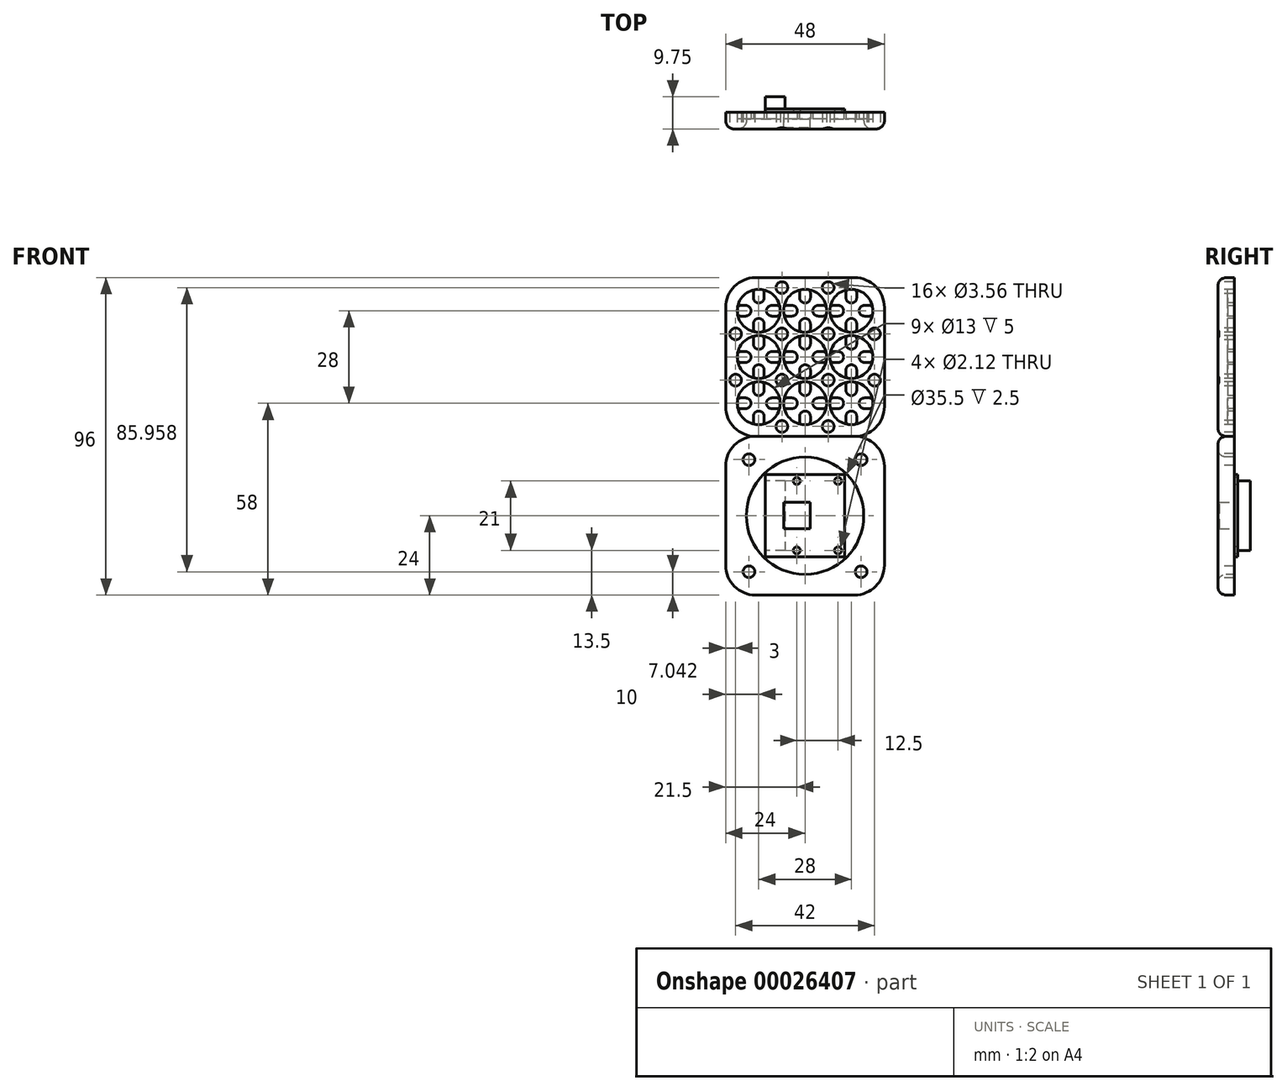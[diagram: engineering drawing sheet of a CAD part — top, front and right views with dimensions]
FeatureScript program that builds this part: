
annotation { "Feature Type Name" : "Feature", "Feature Type Description" : "" }
export const myFeature = defineFeature(function(context is Context, id is Id, definition is map)
    precondition{}
    {
        {
            var Q0;
            Q0=qCreatedBy(makeId("Front.planeOp"),FACE);
            var sketch = newSketch(context, id + "F0", { "sketchPlane" : qUnion([Q0])});
            skCircle(sketch, "E0", {"center": v(0, 0) * mm, "radius": 6.5 * mm});
            skCircle(sketch, "E1", {"center": v(0, 0) * mm, "radius": 7 * mm, "construction": true});
            skLineSegment(sketch, "E2", {"start": v(0, 7) * mm, "end": v(0, 14) * mm, "construction": true});
            skCircle(sketch, "E3", {"center": v(0, 14) * mm, "radius": 7 * mm, "construction": true});
            skCircle(sketch, "E4", {"center": v(0, 14) * mm, "radius": 6.5 * mm});
            skLineSegment(sketch, "E5", {"start": v(0, -7) * mm, "end": v(0, -14) * mm, "construction": true});
            skCircle(sketch, "E6", {"center": v(0, -14) * mm, "radius": 7 * mm, "construction": true});
            skCircle(sketch, "E7", {"center": v(0, -14) * mm, "radius": 6.5 * mm});
            skLineSegment(sketch, "E8", {"start": v(-7, 14) * mm, "end": v(-14, 14) * mm, "construction": true});
            skLineSegment(sketch, "E9", {"start": v(-7, 0) * mm, "end": v(-14, 0) * mm, "construction": true});
            skLineSegment(sketch, "E10", {"start": v(-7, -14) * mm, "end": v(-14, -14) * mm, "construction": true});
            skLineSegment(sketch, "E11", {"start": v(7, 14) * mm, "end": v(14, 14) * mm, "construction": true});
            skLineSegment(sketch, "E12", {"start": v(7, 0) * mm, "end": v(14, 0) * mm, "construction": true});
            skLineSegment(sketch, "E13", {"start": v(7, -14) * mm, "end": v(14, -14) * mm, "construction": true});
            skCircle(sketch, "E14", {"center": v(14, 14) * mm, "radius": 7 * mm, "construction": true});
            skCircle(sketch, "E15", {"center": v(14, 0) * mm, "radius": 7 * mm, "construction": true});
            skCircle(sketch, "E16", {"center": v(14, -14) * mm, "radius": 7 * mm, "construction": true});
            skCircle(sketch, "E17", {"center": v(-14, -14) * mm, "radius": 7 * mm, "construction": true});
            skCircle(sketch, "E18", {"center": v(-14, 0) * mm, "radius": 7 * mm, "construction": true});
            skCircle(sketch, "E19", {"center": v(-14, 14) * mm, "radius": 7 * mm, "construction": true});
            skCircle(sketch, "E20", {"center": v(-14, 14) * mm, "radius": 6.5 * mm});
            skCircle(sketch, "E21", {"center": v(-14, 0) * mm, "radius": 6.5 * mm});
            skCircle(sketch, "E22", {"center": v(-14, -14) * mm, "radius": 6.5 * mm});
            skCircle(sketch, "E23", {"center": v(14, -14) * mm, "radius": 6.5 * mm});
            skCircle(sketch, "E24", {"center": v(14, 0) * mm, "radius": 6.5 * mm});
            skCircle(sketch, "E25", {"center": v(14, 14) * mm, "radius": 6.5 * mm});
            skLineSegment(sketch, "E26", {"start": v(-14, 14) * mm, "end": v(-21, 14) * mm, "construction": true});
            skLineSegment(sketch, "E27", {"start": v(-14, 14) * mm, "end": v(-14, 21) * mm, "construction": true});
            skLineSegment(sketch, "E28", {"start": v(14, -14) * mm, "end": v(14, -21) * mm, "construction": true});
            skLineSegment(sketch, "E29", {"start": v(14, -14) * mm, "end": v(21, -14) * mm, "construction": true});
            skLineSegment(sketch, "E30.rect.bottom", {"start": v(-21, 21) * mm, "end": v(21, 21) * mm, "construction": true});
            skLineSegment(sketch, "E30.rect.top", {"start": v(-12, -21) * mm, "end": v(21, -21) * mm, "construction": true});
            skLineSegment(sketch, "E30.rect.left", {"start": v(-21, 21) * mm, "end": v(-21, -12) * mm, "construction": true});
            skLineSegment(sketch, "E30.rect.right", {"start": v(21, 21) * mm, "end": v(21, -21) * mm, "construction": true});
            skLineSegment(sketch, "E31.0", {"start": v(-24, 15) * mm, "end": v(-24, -15) * mm});
            skLineSegment(sketch, "E31.1", {"start": v(-15, 24) * mm, "end": v(15, 24) * mm});
            skLineSegment(sketch, "E31.2", {"start": v(24, 15) * mm, "end": v(24, -15) * mm});
            skLineSegment(sketch, "E31.3", {"start": v(-15, -24) * mm, "end": v(15, -24) * mm});
            skPoint(sketch, "E32.visualSharp", {"position": v(-24, -24) * mm});
            skArc(sketch, "E32.filletArc", {"start": v(-24, -15) * mm, "mid": v(-21.36, -21.36) * mm, "end": v(-15, -24) * mm});
            skPoint(sketch, "E33.visualSharp", {"position": v(-24, 24) * mm});
            skArc(sketch, "E33.filletArc", {"start": v(-15, 24) * mm, "mid": v(-21.36, 21.36) * mm, "end": v(-24, 15) * mm});
            skPoint(sketch, "E34.visualSharp", {"position": v(24, 24) * mm});
            skArc(sketch, "E34.filletArc", {"start": v(24, 15) * mm, "mid": v(21.36, 21.36) * mm, "end": v(15, 24) * mm});
            skPoint(sketch, "E35.visualSharp", {"position": v(24, -24) * mm});
            skArc(sketch, "E35.filletArc", {"start": v(15, -24) * mm, "mid": v(21.36, -21.36) * mm, "end": v(24, -15) * mm});
            skPoint(sketch, "E36.visualSharp", {"position": v(-21, -21) * mm});
            skArc(sketch, "E36.filletArc", {"start": v(-21, -12) * mm, "mid": v(-18.36, -18.36) * mm, "end": v(-12, -21) * mm, "construction": true});
            skLineSegment(sketch, "E37", {"start": v(7, -14) * mm, "end": v(7, 14) * mm, "construction": true});
            skLineSegment(sketch, "E38", {"start": v(14, -7) * mm, "end": v(-14, -7) * mm, "construction": true});
            skLineSegment(sketch, "E39", {"start": v(-7, -14) * mm, "end": v(-7, 14) * mm, "construction": true});
            skLineSegment(sketch, "E40", {"start": v(14, -7) * mm, "end": v(24, -7) * mm, "construction": true});
            skLineSegment(sketch, "E41", {"start": v(7, -14) * mm, "end": v(7, -24) * mm, "construction": true});
            skLineSegment(sketch, "E42", {"start": v(-7, -14) * mm, "end": v(-7, -24) * mm, "construction": true});
            skLineSegment(sketch, "E43", {"start": v(-14, -7) * mm, "end": v(-24, -7) * mm, "construction": true});
            skLineSegment(sketch, "E44", {"start": v(14, 7) * mm, "end": v(-14, 7) * mm, "construction": true});
            skLineSegment(sketch, "E45", {"start": v(14, 7) * mm, "end": v(24, 7) * mm, "construction": true});
            skLineSegment(sketch, "E46", {"start": v(7, 14) * mm, "end": v(7, 24) * mm, "construction": true});
            skLineSegment(sketch, "E47", {"start": v(-7, 14) * mm, "end": v(-7, 24) * mm, "construction": true});
            skLineSegment(sketch, "E48", {"start": v(-14, 7) * mm, "end": v(-24, 7) * mm, "construction": true});
            skCircle(sketch, "E49", {"center": v(7, -7) * mm, "radius": 1.78 * mm});
            skCircle(sketch, "E50", {"center": v(-7, -7) * mm, "radius": 1.78 * mm});
            skCircle(sketch, "E51", {"center": v(-7, 7) * mm, "radius": 1.78 * mm});
            skCircle(sketch, "E52", {"center": v(7, 7) * mm, "radius": 1.78 * mm});
            skCircle(sketch, "E53", {"center": v(-7, -21) * mm, "radius": 1.78 * mm});
            skCircle(sketch, "E54", {"center": v(7, -21) * mm, "radius": 1.78 * mm});
            skCircle(sketch, "E55", {"center": v(21, -7) * mm, "radius": 1.78 * mm});
            skCircle(sketch, "E56", {"center": v(21, 7) * mm, "radius": 1.78 * mm});
            skCircle(sketch, "E57", {"center": v(7, 21) * mm, "radius": 1.78 * mm});
            skCircle(sketch, "E58", {"center": v(-7, 21) * mm, "radius": 1.78 * mm});
            skCircle(sketch, "E59", {"center": v(-21, 7) * mm, "radius": 1.78 * mm});
            skCircle(sketch, "E60", {"center": v(-21, -7) * mm, "radius": 1.78 * mm});
            skSolve(sketch);
        }
        {
            var Q0;
            Q0=makeQuery(id+"F0.imprint","IMPRINT",FACE,{"disambiguationData":[TD([[makeQuery(id+"F0.imprint","IMPRINT",EDGE,{"derivedFrom":sQuery(id+"F0.wireOp",EDGE,"E0")}),-1.0]])]});
            var Q1;
            Q1=makeQuery(id+"F0.imprint","IMPRINT",FACE,{"disambiguationData":[TD([[makeQuery(id+"F0.imprint","IMPRINT",EDGE,{"derivedFrom":sQuery(id+"F0.wireOp",EDGE,"E21")}),1.0]])]});
            var Q2;
            Q2=makeQuery(id+"F0.imprint","IMPRINT",FACE,{"disambiguationData":[TD([[makeQuery(id+"F0.imprint","IMPRINT",EDGE,{"derivedFrom":sQuery(id+"F0.wireOp",EDGE,"E22")}),1.0]])]});
            var Q3;
            Q3=makeQuery(id+"F0.imprint","IMPRINT",FACE,{"disambiguationData":[TD([[makeQuery(id+"F0.imprint","IMPRINT",EDGE,{"derivedFrom":sQuery(id+"F0.wireOp",EDGE,"E7")}),1.0]])]});
            var Q4;
            Q4=makeQuery(id+"F0.imprint","IMPRINT",FACE,{"disambiguationData":[TD([[makeQuery(id+"F0.imprint","IMPRINT",EDGE,{"derivedFrom":sQuery(id+"F0.wireOp",EDGE,"E0")}),1.0]])]});
            var Q5;
            Q5=makeQuery(id+"F0.imprint","IMPRINT",FACE,{"disambiguationData":[TD([[makeQuery(id+"F0.imprint","IMPRINT",EDGE,{"derivedFrom":sQuery(id+"F0.wireOp",EDGE,"E20")}),1.0]])]});
            var Q6;
            Q6=makeQuery(id+"F0.imprint","IMPRINT",FACE,{"disambiguationData":[TD([[makeQuery(id+"F0.imprint","IMPRINT",EDGE,{"derivedFrom":sQuery(id+"F0.wireOp",EDGE,"E4")}),1.0]])]});
            var Q7;
            Q7=makeQuery(id+"F0.imprint","IMPRINT",FACE,{"disambiguationData":[TD([[makeQuery(id+"F0.imprint","IMPRINT",EDGE,{"derivedFrom":sQuery(id+"F0.wireOp",EDGE,"E25")}),1.0]])]});
            var Q8;
            Q8=makeQuery(id+"F0.imprint","IMPRINT",FACE,{"disambiguationData":[TD([[makeQuery(id+"F0.imprint","IMPRINT",EDGE,{"derivedFrom":sQuery(id+"F0.wireOp",EDGE,"E24")}),1.0]])]});
            var Q9;
            Q9=makeQuery(id+"F0.imprint","IMPRINT",FACE,{"disambiguationData":[TD([[makeQuery(id+"F0.imprint","IMPRINT",EDGE,{"derivedFrom":sQuery(id+"F0.wireOp",EDGE,"E23")}),1.0]])]});
            extrude(context, id + "F1", {"entities" : qUnion([Q0, Q1, Q2, Q3, Q4, Q5, Q6, Q7, Q8, Q9]), "oppositeDirection" : true, "depth" : 5 * mm});
        }
        {
            var Q0;
            Q0=makeQuery(id+"F0.imprint","IMPRINT",FACE,{"disambiguationData":[TD([[makeQuery(id+"F0.imprint","IMPRINT",EDGE,{"derivedFrom":sQuery(id+"F0.wireOp",EDGE,"E22")}),1.0]])]});
            var Q1;
            Q1=makeQuery(id+"F0.imprint","IMPRINT",FACE,{"disambiguationData":[TD([[makeQuery(id+"F0.imprint","IMPRINT",EDGE,{"derivedFrom":sQuery(id+"F0.wireOp",EDGE,"E21")}),1.0]])]});
            var Q2;
            Q2=makeQuery(id+"F0.imprint","IMPRINT",FACE,{"disambiguationData":[TD([[makeQuery(id+"F0.imprint","IMPRINT",EDGE,{"derivedFrom":sQuery(id+"F0.wireOp",EDGE,"E20")}),1.0]])]});
            var Q3;
            Q3=makeQuery(id+"F0.imprint","IMPRINT",FACE,{"disambiguationData":[TD([[makeQuery(id+"F0.imprint","IMPRINT",EDGE,{"derivedFrom":sQuery(id+"F0.wireOp",EDGE,"E4")}),1.0]])]});
            var Q4;
            Q4=makeQuery(id+"F0.imprint","IMPRINT",FACE,{"disambiguationData":[TD([[makeQuery(id+"F0.imprint","IMPRINT",EDGE,{"derivedFrom":sQuery(id+"F0.wireOp",EDGE,"E25")}),1.0]])]});
            var Q5;
            Q5=makeQuery(id+"F0.imprint","IMPRINT",FACE,{"disambiguationData":[TD([[makeQuery(id+"F0.imprint","IMPRINT",EDGE,{"derivedFrom":sQuery(id+"F0.wireOp",EDGE,"E24")}),1.0]])]});
            var Q6;
            Q6=makeQuery(id+"F0.imprint","IMPRINT",FACE,{"disambiguationData":[TD([[makeQuery(id+"F0.imprint","IMPRINT",EDGE,{"derivedFrom":sQuery(id+"F0.wireOp",EDGE,"E23")}),1.0]])]});
            var Q7;
            Q7=makeQuery(id+"F0.imprint","IMPRINT",FACE,{"disambiguationData":[TD([[makeQuery(id+"F0.imprint","IMPRINT",EDGE,{"derivedFrom":sQuery(id+"F0.wireOp",EDGE,"E7")}),1.0]])]});
            var Q8;
            Q8=makeQuery(id+"F0.imprint","IMPRINT",FACE,{"disambiguationData":[TD([[makeQuery(id+"F0.imprint","IMPRINT",EDGE,{"derivedFrom":sQuery(id+"F0.wireOp",EDGE,"E0")}),1.0]])]});
            extrude(context, id + "F2", {"entities" : qUnion([Q0, Q1, Q2, Q3, Q4, Q5, Q6, Q7, Q8]), "operationType" : NewBodyOperationType.REMOVE, "oppositeDirection" : true, "depth" : 3 * mm});
        }
        {
            var Q0;
            Q0=makeQuery(id+"F1.opExtrude","CAP_EDGE",EDGE,{"disambiguationData":[OSD([sQuery(id+"F0.wireOp",EDGE,"E31.3")])],"isStart":true});
            fillet(context, id + "F3", {"entities" : qUnion([Q0]), "radius" : 2.5 * mm, "tangentPropagation" : true, "allowEdgeOverflow" : false});
        }
        {
            var Q0;
            Q0=makeQuery(id+"F0.imprint","IMPRINT",FACE,{"disambiguationData":[TD([[makeQuery(id+"F0.imprint","IMPRINT",EDGE,{"derivedFrom":sQuery(id+"F0.wireOp",EDGE,"E0")}),1.0]])]});
            var sketch = newSketch(context, id + "F4", { "sketchPlane" : qUnion([Q0])});
            skCircle(sketch, "E61.0", {"center": v(-14, 14) * mm, "radius": 6.5 * mm, "construction": true});
            skCircle(sketch, "E62.0", {"center": v(0, 14) * mm, "radius": 6.5 * mm, "construction": true});
            skCircle(sketch, "E63.0", {"center": v(14, 14) * mm, "radius": 6.5 * mm, "construction": true});
            skCircle(sketch, "E64.0", {"center": v(-14, 0) * mm, "radius": 6.5 * mm, "construction": true});
            skCircle(sketch, "E65.0", {"center": v(0, 0) * mm, "radius": 6.5 * mm, "construction": true});
            skCircle(sketch, "E66.0", {"center": v(14, 0) * mm, "radius": 6.5 * mm, "construction": true});
            skCircle(sketch, "E67.0", {"center": v(14, -14) * mm, "radius": 6.5 * mm, "construction": true});
            skCircle(sketch, "E68.0", {"center": v(0, -14) * mm, "radius": 6.5 * mm, "construction": true});
            skCircle(sketch, "E69.0", {"center": v(-14, -14) * mm, "radius": 6.5 * mm, "construction": true});
            skLineSegment(sketch, "E70", {"start": v(0, 0) * mm, "end": v(0, 6.5) * mm, "construction": true});
            skLineSegment(sketch, "E71", {"start": v(0, 0) * mm, "end": v(0, -6.5) * mm, "construction": true});
            skLineSegment(sketch, "E72", {"start": v(0, 0) * mm, "end": v(6.5, 0) * mm, "construction": true});
            skLineSegment(sketch, "E73", {"start": v(0, 0) * mm, "end": v(-6.5, 0) * mm, "construction": true});
            skLineSegment(sketch, "E74", {"start": v(0, 3.25) * mm, "end": v(-3.25, 0) * mm, "construction": true});
            skLineSegment(sketch, "E75", {"start": v(-3.25, 0) * mm, "end": v(0, -3.25) * mm, "construction": true});
            skLineSegment(sketch, "E76", {"start": v(0, -3.25) * mm, "end": v(3.25, 0) * mm, "construction": true});
            skLineSegment(sketch, "E77", {"start": v(3.25, 0) * mm, "end": v(0, 3.25) * mm, "construction": true});
            skLineSegment(sketch, "E78", {"start": v(1.62, 1.63) * mm, "end": v(1.62, 6.3) * mm, "construction": true});
            skLineSegment(sketch, "E79", {"start": v(-1.63, 1.63) * mm, "end": v(-1.63, 6.3) * mm, "construction": true});
            skLineSegment(sketch, "E80", {"start": v(1.62, 1.63) * mm, "end": v(6.3, 1.63) * mm, "construction": true});
            skLineSegment(sketch, "E81", {"start": v(1.63, -1.63) * mm, "end": v(6.3, -1.63) * mm, "construction": true});
            skLineSegment(sketch, "E82", {"start": v(1.63, -1.63) * mm, "end": v(1.63, -6.3) * mm, "construction": true});
            skLineSegment(sketch, "E83", {"start": v(-1.63, -1.62) * mm, "end": v(-1.63, -6.3) * mm, "construction": true});
            skLineSegment(sketch, "E84", {"start": v(-1.63, -1.62) * mm, "end": v(-6.3, -1.62) * mm, "construction": true});
            skLineSegment(sketch, "E85", {"start": v(-1.63, 1.63) * mm, "end": v(-6.3, 1.63) * mm, "construction": true});
            skLineSegment(sketch, "E86", {"start": v(1.63, 3.96) * mm, "end": v(-1.63, 3.96) * mm, "construction": true});
            skLineSegment(sketch, "E87", {"start": v(3.96, 1.63) * mm, "end": v(3.96, -1.63) * mm, "construction": true});
            skLineSegment(sketch, "E88", {"start": v(1.63, -3.96) * mm, "end": v(-1.63, -3.96) * mm, "construction": true});
            skLineSegment(sketch, "E89", {"start": v(-3.96, 1.63) * mm, "end": v(-3.96, -1.62) * mm, "construction": true});
            skCircle(sketch, "E90", {"center": v(3.96, 0) * mm, "radius": 1.63 * mm, "construction": true});
            skCircle(sketch, "E91", {"center": v(0, 3.96) * mm, "radius": 1.63 * mm, "construction": true});
            skCircle(sketch, "E92", {"center": v(-3.96, 0) * mm, "radius": 1.63 * mm, "construction": true});
            skCircle(sketch, "E93", {"center": v(0, -3.96) * mm, "radius": 1.63 * mm, "construction": true});
            skLineSegment(sketch, "E94", {"start": v(6.3, 1.63) * mm, "end": v(3.96, 1.63) * mm});
            skLineSegment(sketch, "E95", {"start": v(6.3, -1.63) * mm, "end": v(3.96, -1.63) * mm});
            skArc(sketch, "E96", {"start": v(6.3, -1.63) * mm, "mid": v(6.5, 0) * mm, "end": v(6.3, 1.63) * mm});
            skArc(sketch, "E97", {"start": v(3.96, 1.63) * mm, "mid": v(2.33, 0) * mm, "end": v(3.96, -1.63) * mm});
            skArc(sketch, "E98", {"start": v(-1.63, 3.96) * mm, "mid": v(0, 2.33) * mm, "end": v(1.63, 3.96) * mm});
            skArc(sketch, "E99", {"start": v(1.63, 6.3) * mm, "mid": v(0, 6.5) * mm, "end": v(-1.63, 6.3) * mm});
            skLineSegment(sketch, "E100", {"start": v(1.63, 6.3) * mm, "end": v(1.63, 3.96) * mm});
            skLineSegment(sketch, "E101", {"start": v(-1.63, 6.3) * mm, "end": v(-1.63, 3.96) * mm});
            skLineSegment(sketch, "E102", {"start": v(1.63, -3.96) * mm, "end": v(1.63, -6.3) * mm});
            skLineSegment(sketch, "E103", {"start": v(-1.63, -6.3) * mm, "end": v(-1.63, -3.96) * mm});
            skLineSegment(sketch, "E104", {"start": v(-3.96, -1.62) * mm, "end": v(-6.3, -1.62) * mm});
            skLineSegment(sketch, "E105", {"start": v(-3.96, 1.63) * mm, "end": v(-6.3, 1.63) * mm});
            skArc(sketch, "E106", {"start": v(-3.96, -1.62) * mm, "mid": v(-2.33, 0) * mm, "end": v(-3.96, 1.63) * mm});
            skArc(sketch, "E107", {"start": v(-6.3, 1.62) * mm, "mid": v(-6.5, 0) * mm, "end": v(-6.3, -1.62) * mm});
            skArc(sketch, "E108", {"start": v(1.63, -3.96) * mm, "mid": v(0, -2.33) * mm, "end": v(-1.63, -3.96) * mm});
            skArc(sketch, "E109", {"start": v(-1.63, -6.3) * mm, "mid": v(0, -6.5) * mm, "end": v(1.63, -6.3) * mm});
            skLineSegment(sketch, "E110.1.0.0", {"start": v(20.3, 1.63) * mm, "end": v(17.96, 1.63) * mm});
            skArc(sketch, "E110.1.0.1", {"start": v(20.3, -1.63) * mm, "mid": v(20.5, 0) * mm, "end": v(20.3, 1.62) * mm});
            skLineSegment(sketch, "E110.1.0.2", {"start": v(20.3, -1.63) * mm, "end": v(17.96, -1.63) * mm});
            skArc(sketch, "E110.1.0.3", {"start": v(17.96, 1.63) * mm, "mid": v(16.33, 0) * mm, "end": v(17.96, -1.63) * mm});
            skArc(sketch, "E110.1.0.4", {"start": v(12.38, 3.96) * mm, "mid": v(14, 2.33) * mm, "end": v(15.62, 3.96) * mm});
            skLineSegment(sketch, "E110.1.0.5", {"start": v(15.62, 6.3) * mm, "end": v(15.62, 3.96) * mm});
            skLineSegment(sketch, "E110.1.0.6", {"start": v(12.38, 6.3) * mm, "end": v(12.38, 3.96) * mm});
            skArc(sketch, "E110.1.0.7", {"start": v(15.62, 6.3) * mm, "mid": v(14, 6.5) * mm, "end": v(12.37, 6.3) * mm});
            skLineSegment(sketch, "E110.1.0.8", {"start": v(10.04, 1.63) * mm, "end": v(7.7, 1.63) * mm});
            skArc(sketch, "E110.1.0.9", {"start": v(10.04, -1.62) * mm, "mid": v(11.67, 0) * mm, "end": v(10.04, 1.63) * mm});
            skLineSegment(sketch, "E110.1.0.10", {"start": v(10.04, -1.62) * mm, "end": v(7.7, -1.62) * mm});
            skArc(sketch, "E110.1.0.11", {"start": v(7.7, 1.62) * mm, "mid": v(7.5, 0) * mm, "end": v(7.7, -1.62) * mm});
            skArc(sketch, "E110.1.0.12", {"start": v(15.62, -3.96) * mm, "mid": v(14, -2.33) * mm, "end": v(12.38, -3.96) * mm});
            skLineSegment(sketch, "E110.1.0.13", {"start": v(15.62, -3.96) * mm, "end": v(15.62, -6.3) * mm});
            skLineSegment(sketch, "E110.1.0.14", {"start": v(12.38, -6.3) * mm, "end": v(12.38, -3.96) * mm});
            skArc(sketch, "E110.1.0.15", {"start": v(12.37, -6.3) * mm, "mid": v(14, -6.5) * mm, "end": v(15.62, -6.3) * mm});
            skLineSegment(sketch, "E110.direction1", {"start": v(3.96, 1.63) * mm, "end": v(17.96, 1.63) * mm, "construction": true});
            skArc(sketch, "E111.1.0.0", {"start": v(-10.04, 1.63) * mm, "mid": v(-11.67, 0) * mm, "end": v(-10.04, -1.63) * mm});
            skLineSegment(sketch, "E111.1.0.1", {"start": v(-7.7, 1.63) * mm, "end": v(-10.04, 1.63) * mm});
            skArc(sketch, "E111.1.0.2", {"start": v(-7.7, -1.63) * mm, "mid": v(-7.5, 0) * mm, "end": v(-7.7, 1.63) * mm});
            skLineSegment(sketch, "E111.1.0.3", {"start": v(-7.7, -1.63) * mm, "end": v(-10.04, -1.63) * mm});
            skArc(sketch, "E111.1.0.4", {"start": v(-15.62, 3.96) * mm, "mid": v(-14, 2.33) * mm, "end": v(-12.38, 3.96) * mm});
            skLineSegment(sketch, "E111.1.0.5", {"start": v(-12.38, 6.3) * mm, "end": v(-12.38, 3.96) * mm});
            skArc(sketch, "E111.1.0.6", {"start": v(-12.38, 6.3) * mm, "mid": v(-14, 6.5) * mm, "end": v(-15.62, 6.3) * mm});
            skLineSegment(sketch, "E111.1.0.7", {"start": v(-15.62, 6.3) * mm, "end": v(-15.62, 3.96) * mm});
            skLineSegment(sketch, "E111.1.0.8", {"start": v(-17.96, 1.63) * mm, "end": v(-20.3, 1.63) * mm});
            skArc(sketch, "E111.1.0.9", {"start": v(-17.96, -1.62) * mm, "mid": v(-16.33, 0) * mm, "end": v(-17.96, 1.63) * mm});
            skLineSegment(sketch, "E111.1.0.10", {"start": v(-17.96, -1.62) * mm, "end": v(-20.3, -1.62) * mm});
            skArc(sketch, "E111.1.0.11", {"start": v(-20.3, 1.62) * mm, "mid": v(-20.5, 0) * mm, "end": v(-20.3, -1.62) * mm});
            skArc(sketch, "E111.1.0.12", {"start": v(-12.38, -3.96) * mm, "mid": v(-14, -2.33) * mm, "end": v(-15.62, -3.96) * mm});
            skLineSegment(sketch, "E111.1.0.13", {"start": v(-12.38, -3.96) * mm, "end": v(-12.38, -6.3) * mm});
            skArc(sketch, "E111.1.0.14", {"start": v(-15.62, -6.3) * mm, "mid": v(-14, -6.5) * mm, "end": v(-12.38, -6.3) * mm});
            skLineSegment(sketch, "E111.1.0.15", {"start": v(-15.62, -6.3) * mm, "end": v(-15.62, -3.96) * mm});
            skLineSegment(sketch, "E111.direction1", {"start": v(3.96, -1.63) * mm, "end": v(-10.04, -1.63) * mm, "construction": true});
            skCircle(sketch, "E112.0", {"center": v(21, 7) * mm, "radius": 1.78 * mm, "construction": true});
            skCircle(sketch, "E113.0", {"center": v(21, -7) * mm, "radius": 1.78 * mm, "construction": true});
            skCircle(sketch, "E114.0", {"center": v(7, 21) * mm, "radius": 1.78 * mm, "construction": true});
            skCircle(sketch, "E115.0", {"center": v(-7, 21) * mm, "radius": 1.78 * mm, "construction": true});
            skCircle(sketch, "E116.0", {"center": v(7, 7) * mm, "radius": 1.78 * mm, "construction": true});
            skCircle(sketch, "E117.0", {"center": v(-7, 7) * mm, "radius": 1.78 * mm, "construction": true});
            skCircle(sketch, "E118.0", {"center": v(-21, 7) * mm, "radius": 1.78 * mm, "construction": true});
            skCircle(sketch, "E119.0", {"center": v(-21, -7) * mm, "radius": 1.78 * mm, "construction": true});
            skCircle(sketch, "E120.0", {"center": v(-7, -7) * mm, "radius": 1.78 * mm, "construction": true});
            skCircle(sketch, "E121.0", {"center": v(7, -7) * mm, "radius": 1.78 * mm, "construction": true});
            skCircle(sketch, "E122.0", {"center": v(7, -21) * mm, "radius": 1.78 * mm, "construction": true});
            skCircle(sketch, "E123.0", {"center": v(-7, -21) * mm, "radius": 1.78 * mm, "construction": true});
            skLineSegment(sketch, "E124", {"start": v(14, -14) * mm, "end": v(-14, -14) * mm, "construction": true});
            skLineSegment(sketch, "E125", {"start": v(14, 14) * mm, "end": v(-14, 14) * mm, "construction": true});
            skLineSegment(sketch, "E126", {"start": v(14, 14) * mm, "end": v(14, -14) * mm, "construction": true});
            skLineSegment(sketch, "E127", {"start": v(-14, -14) * mm, "end": v(-14, 14) * mm, "construction": true});
            skLineSegment(sketch, "E128", {"start": v(21, -7) * mm, "end": v(-21, -7) * mm, "construction": true});
            skLineSegment(sketch, "E129", {"start": v(21, 7) * mm, "end": v(-21, 7) * mm, "construction": true});
            skLineSegment(sketch, "E130", {"start": v(7, 21) * mm, "end": v(7, -21) * mm, "construction": true});
            skLineSegment(sketch, "E131", {"start": v(-7, 21) * mm, "end": v(-7, -21) * mm, "construction": true});
            skArc(sketch, "E132.MirrorCS", {"start": v(7.7, 12.38) * mm, "mid": v(7.5, 14) * mm, "end": v(7.7, 15.62) * mm});
            skLineSegment(sketch, "E133.MirrorCS", {"start": v(10.04, 15.62) * mm, "end": v(7.7, 15.62) * mm});
            skArc(sketch, "E134.MirrorCS", {"start": v(10.04, 15.62) * mm, "mid": v(11.67, 14) * mm, "end": v(10.04, 12.38) * mm});
            skLineSegment(sketch, "E135.MirrorCS", {"start": v(10.04, 12.38) * mm, "end": v(7.7, 12.38) * mm});
            skArc(sketch, "E136.MirrorCS", {"start": v(12.38, 10.04) * mm, "mid": v(14, 11.67) * mm, "end": v(15.62, 10.04) * mm});
            skArc(sketch, "E137.MirrorCS", {"start": v(15.62, 7.7) * mm, "mid": v(14, 7.5) * mm, "end": v(12.37, 7.7) * mm});
            skLineSegment(sketch, "E138.MirrorCS", {"start": v(15.62, 7.7) * mm, "end": v(15.62, 10.04) * mm});
            skLineSegment(sketch, "E139.MirrorCS", {"start": v(12.38, 7.7) * mm, "end": v(12.38, 10.04) * mm});
            skLineSegment(sketch, "E140.MirrorCS", {"start": v(12.38, 20.3) * mm, "end": v(12.38, 17.96) * mm});
            skArc(sketch, "E141.MirrorCS", {"start": v(12.37, 20.3) * mm, "mid": v(14, 20.5) * mm, "end": v(15.62, 20.3) * mm});
            skLineSegment(sketch, "E142.MirrorCS", {"start": v(15.62, 17.96) * mm, "end": v(15.62, 20.3) * mm});
            skArc(sketch, "E143.MirrorCS", {"start": v(15.62, 17.96) * mm, "mid": v(14, 16.33) * mm, "end": v(12.38, 17.96) * mm});
            skArc(sketch, "E144.MirrorCS", {"start": v(17.96, 12.38) * mm, "mid": v(16.33, 14) * mm, "end": v(17.96, 15.62) * mm});
            skLineSegment(sketch, "E145.MirrorCS", {"start": v(20.3, 15.62) * mm, "end": v(17.96, 15.62) * mm});
            skLineSegment(sketch, "E146.MirrorCS", {"start": v(20.3, 12.38) * mm, "end": v(17.96, 12.38) * mm});
            skArc(sketch, "E147.MirrorCS", {"start": v(20.3, 15.62) * mm, "mid": v(20.5, 14) * mm, "end": v(20.3, 12.38) * mm});
            skLineSegment(sketch, "E148.MirrorCS", {"start": v(6.3, 12.38) * mm, "end": v(3.96, 12.38) * mm});
            skArc(sketch, "E149.MirrorCS", {"start": v(3.96, 12.38) * mm, "mid": v(2.33, 14) * mm, "end": v(3.96, 15.62) * mm});
            skArc(sketch, "E150.MirrorCS", {"start": v(6.3, 15.62) * mm, "mid": v(6.5, 14) * mm, "end": v(6.3, 12.38) * mm});
            skLineSegment(sketch, "E151.MirrorCS", {"start": v(6.3, 15.62) * mm, "end": v(3.96, 15.62) * mm});
            skLineSegment(sketch, "E152.MirrorCS", {"start": v(1.63, 7.7) * mm, "end": v(1.63, 10.04) * mm});
            skArc(sketch, "E153.MirrorCS", {"start": v(1.63, 7.7) * mm, "mid": v(0, 7.5) * mm, "end": v(-1.63, 7.7) * mm});
            skLineSegment(sketch, "E154.MirrorCS", {"start": v(-1.63, 7.7) * mm, "end": v(-1.63, 10.04) * mm});
            skArc(sketch, "E155.MirrorCS", {"start": v(-1.63, 10.04) * mm, "mid": v(0, 11.67) * mm, "end": v(1.63, 10.04) * mm});
            skArc(sketch, "E156.MirrorCS", {"start": v(1.63, 17.96) * mm, "mid": v(0, 16.33) * mm, "end": v(-1.63, 17.96) * mm});
            skLineSegment(sketch, "E157.MirrorCS", {"start": v(1.63, 17.96) * mm, "end": v(1.63, 20.3) * mm});
            skLineSegment(sketch, "E158.MirrorCS", {"start": v(-1.63, 20.3) * mm, "end": v(-1.63, 17.96) * mm});
            skArc(sketch, "E159.MirrorCS", {"start": v(-1.63, 20.3) * mm, "mid": v(0, 20.5) * mm, "end": v(1.63, 20.3) * mm});
            skLineSegment(sketch, "E160.MirrorCS", {"start": v(-3.96, 12.38) * mm, "end": v(-6.3, 12.38) * mm});
            skArc(sketch, "E161.MirrorCS", {"start": v(-3.96, 15.62) * mm, "mid": v(-2.33, 14) * mm, "end": v(-3.96, 12.38) * mm});
            skLineSegment(sketch, "E162.MirrorCS", {"start": v(-3.96, 15.62) * mm, "end": v(-6.3, 15.62) * mm});
            skArc(sketch, "E163.MirrorCS", {"start": v(-6.3, 12.38) * mm, "mid": v(-6.5, 14) * mm, "end": v(-6.3, 15.62) * mm});
            skLineSegment(sketch, "E164.MirrorCS", {"start": v(-7.7, 12.38) * mm, "end": v(-10.04, 12.38) * mm});
            skArc(sketch, "E165.MirrorCS", {"start": v(-7.7, 15.62) * mm, "mid": v(-7.5, 14) * mm, "end": v(-7.7, 12.38) * mm});
            skLineSegment(sketch, "E166.MirrorCS", {"start": v(-7.7, 15.62) * mm, "end": v(-10.04, 15.62) * mm});
            skArc(sketch, "E167.MirrorCS", {"start": v(-10.04, 12.38) * mm, "mid": v(-11.67, 14) * mm, "end": v(-10.04, 15.62) * mm});
            skArc(sketch, "E168.MirrorCS", {"start": v(-15.62, 10.04) * mm, "mid": v(-14, 11.67) * mm, "end": v(-12.38, 10.04) * mm});
            skLineSegment(sketch, "E169.MirrorCS", {"start": v(-12.38, 7.7) * mm, "end": v(-12.38, 10.04) * mm});
            skArc(sketch, "E170.MirrorCS", {"start": v(-12.38, 7.7) * mm, "mid": v(-14, 7.5) * mm, "end": v(-15.62, 7.7) * mm});
            skLineSegment(sketch, "E171.MirrorCS", {"start": v(-15.62, 7.7) * mm, "end": v(-15.62, 10.04) * mm});
            skLineSegment(sketch, "E172.MirrorCS", {"start": v(-17.96, 12.38) * mm, "end": v(-20.3, 12.38) * mm});
            skArc(sketch, "E173.MirrorCS", {"start": v(-17.96, 15.62) * mm, "mid": v(-16.33, 14) * mm, "end": v(-17.96, 12.38) * mm});
            skLineSegment(sketch, "E174.MirrorCS", {"start": v(-17.96, 15.62) * mm, "end": v(-20.3, 15.62) * mm});
            skArc(sketch, "E175.MirrorCS", {"start": v(-20.3, 12.38) * mm, "mid": v(-20.5, 14) * mm, "end": v(-20.3, 15.62) * mm});
            skLineSegment(sketch, "E176.MirrorCS", {"start": v(-12.38, 17.96) * mm, "end": v(-12.38, 20.3) * mm});
            skArc(sketch, "E177.MirrorCS", {"start": v(-12.38, 17.96) * mm, "mid": v(-14, 16.33) * mm, "end": v(-15.62, 17.96) * mm});
            skLineSegment(sketch, "E178.MirrorCS", {"start": v(-15.62, 20.3) * mm, "end": v(-15.62, 17.96) * mm});
            skArc(sketch, "E179.MirrorCS", {"start": v(-15.62, 20.3) * mm, "mid": v(-14, 20.5) * mm, "end": v(-12.38, 20.3) * mm});
            skArc(sketch, "E180.MirrorCS", {"start": v(15.62, -20.3) * mm, "mid": v(14, -20.5) * mm, "end": v(12.37, -20.3) * mm});
            skLineSegment(sketch, "E181.MirrorCS", {"start": v(15.62, -20.3) * mm, "end": v(15.62, -17.96) * mm});
            skArc(sketch, "E182.MirrorCS", {"start": v(12.38, -17.96) * mm, "mid": v(14, -16.33) * mm, "end": v(15.62, -17.96) * mm});
            skLineSegment(sketch, "E183.MirrorCS", {"start": v(12.38, -20.3) * mm, "end": v(12.38, -17.96) * mm});
            skLineSegment(sketch, "E184.MirrorCS", {"start": v(20.3, -15.62) * mm, "end": v(17.96, -15.62) * mm});
            skArc(sketch, "E185.MirrorCS", {"start": v(20.3, -12.38) * mm, "mid": v(20.5, -14) * mm, "end": v(20.3, -15.62) * mm});
            skLineSegment(sketch, "E186.MirrorCS", {"start": v(20.3, -12.38) * mm, "end": v(17.96, -12.38) * mm});
            skArc(sketch, "E187.MirrorCS", {"start": v(17.96, -15.62) * mm, "mid": v(16.33, -14) * mm, "end": v(17.96, -12.38) * mm});
            skArc(sketch, "E188.MirrorCS", {"start": v(15.62, -10.04) * mm, "mid": v(14, -11.67) * mm, "end": v(12.38, -10.04) * mm});
            skLineSegment(sketch, "E189.MirrorCS", {"start": v(15.62, -10.04) * mm, "end": v(15.62, -7.7) * mm});
            skArc(sketch, "E190.MirrorCS", {"start": v(12.37, -7.7) * mm, "mid": v(14, -7.5) * mm, "end": v(15.62, -7.7) * mm});
            skLineSegment(sketch, "E191.MirrorCS", {"start": v(12.38, -7.7) * mm, "end": v(12.38, -10.04) * mm});
            skArc(sketch, "E192.MirrorCS", {"start": v(10.04, -12.38) * mm, "mid": v(11.67, -14) * mm, "end": v(10.04, -15.62) * mm});
            skLineSegment(sketch, "E193.MirrorCS", {"start": v(10.04, -15.62) * mm, "end": v(7.7, -15.62) * mm});
            skArc(sketch, "E194.MirrorCS", {"start": v(7.7, -15.62) * mm, "mid": v(7.5, -14) * mm, "end": v(7.7, -12.38) * mm});
            skLineSegment(sketch, "E195.MirrorCS", {"start": v(10.04, -12.38) * mm, "end": v(7.7, -12.38) * mm});
            skArc(sketch, "E196.MirrorCS", {"start": v(6.3, -12.38) * mm, "mid": v(6.5, -14) * mm, "end": v(6.3, -15.62) * mm});
            skLineSegment(sketch, "E197.MirrorCS", {"start": v(6.3, -15.62) * mm, "end": v(3.96, -15.62) * mm});
            skArc(sketch, "E198.MirrorCS", {"start": v(3.96, -15.62) * mm, "mid": v(2.33, -14) * mm, "end": v(3.96, -12.38) * mm});
            skLineSegment(sketch, "E199.MirrorCS", {"start": v(1.63, -20.3) * mm, "end": v(1.63, -17.96) * mm});
            skArc(sketch, "E200.MirrorCS", {"start": v(-1.63, -17.96) * mm, "mid": v(0, -16.33) * mm, "end": v(1.63, -17.96) * mm});
            skLineSegment(sketch, "E201.MirrorCS", {"start": v(-1.63, -20.3) * mm, "end": v(-1.63, -17.96) * mm});
            skArc(sketch, "E202.MirrorCS", {"start": v(1.63, -20.3) * mm, "mid": v(0, -20.5) * mm, "end": v(-1.63, -20.3) * mm});
            skLineSegment(sketch, "E203.MirrorCS", {"start": v(-3.96, -15.62) * mm, "end": v(-6.3, -15.62) * mm});
            skArc(sketch, "E204.MirrorCS", {"start": v(-3.96, -12.38) * mm, "mid": v(-2.33, -14) * mm, "end": v(-3.96, -15.62) * mm});
            skLineSegment(sketch, "E205.MirrorCS", {"start": v(-3.96, -12.38) * mm, "end": v(-6.3, -12.38) * mm});
            skArc(sketch, "E206.MirrorCS", {"start": v(-6.3, -15.62) * mm, "mid": v(-6.5, -14) * mm, "end": v(-6.3, -12.38) * mm});
            skArc(sketch, "E207.MirrorCS", {"start": v(1.63, -10.04) * mm, "mid": v(0, -11.67) * mm, "end": v(-1.63, -10.04) * mm});
            skLineSegment(sketch, "E208.MirrorCS", {"start": v(1.63, -10.04) * mm, "end": v(1.63, -7.7) * mm});
            skLineSegment(sketch, "E209.MirrorCS", {"start": v(-1.63, -7.7) * mm, "end": v(-1.63, -10.04) * mm});
            skArc(sketch, "E210.MirrorCS", {"start": v(-1.63, -7.7) * mm, "mid": v(0, -7.5) * mm, "end": v(1.63, -7.7) * mm});
            skArc(sketch, "E211.MirrorCS", {"start": v(-7.7, -12.38) * mm, "mid": v(-7.5, -14) * mm, "end": v(-7.7, -15.62) * mm});
            skLineSegment(sketch, "E212.MirrorCS", {"start": v(-7.7, -15.62) * mm, "end": v(-10.04, -15.62) * mm});
            skArc(sketch, "E213.MirrorCS", {"start": v(-10.04, -15.62) * mm, "mid": v(-11.67, -14) * mm, "end": v(-10.04, -12.38) * mm});
            skLineSegment(sketch, "E214.MirrorCS", {"start": v(-7.7, -12.38) * mm, "end": v(-10.04, -12.38) * mm});
            skLineSegment(sketch, "E215.MirrorCS", {"start": v(-12.38, -20.3) * mm, "end": v(-12.38, -17.96) * mm});
            skArc(sketch, "E216.MirrorCS", {"start": v(-12.38, -20.3) * mm, "mid": v(-14, -20.5) * mm, "end": v(-15.62, -20.3) * mm});
            skLineSegment(sketch, "E217.MirrorCS", {"start": v(-15.62, -20.3) * mm, "end": v(-15.62, -17.96) * mm});
            skArc(sketch, "E218.MirrorCS", {"start": v(-15.62, -17.96) * mm, "mid": v(-14, -16.33) * mm, "end": v(-12.38, -17.96) * mm});
            skLineSegment(sketch, "E219.MirrorCS", {"start": v(-17.96, -15.62) * mm, "end": v(-20.3, -15.62) * mm});
            skArc(sketch, "E220.MirrorCS", {"start": v(-17.96, -12.38) * mm, "mid": v(-16.33, -14) * mm, "end": v(-17.96, -15.62) * mm});
            skLineSegment(sketch, "E221.MirrorCS", {"start": v(-17.96, -12.38) * mm, "end": v(-20.3, -12.38) * mm});
            skArc(sketch, "E222.MirrorCS", {"start": v(-20.3, -15.62) * mm, "mid": v(-20.5, -14) * mm, "end": v(-20.3, -12.38) * mm});
            skArc(sketch, "E223.MirrorCS", {"start": v(-12.38, -10.04) * mm, "mid": v(-14, -11.67) * mm, "end": v(-15.62, -10.04) * mm});
            skLineSegment(sketch, "E224.MirrorCS", {"start": v(-12.38, -10.04) * mm, "end": v(-12.38, -7.7) * mm});
            skArc(sketch, "E225.MirrorCS", {"start": v(-15.62, -7.7) * mm, "mid": v(-14, -7.5) * mm, "end": v(-12.38, -7.7) * mm});
            skLineSegment(sketch, "E226.MirrorCS", {"start": v(-15.62, -7.7) * mm, "end": v(-15.62, -10.04) * mm});
            skLineSegment(sketch, "E227", {"start": v(6.3, -12.38) * mm, "end": v(3.96, -12.38) * mm});
            skSolve(sketch);
        }
        {
            var Q0;
            Q0 = qSketchRegion(id + "F4", true);
            extrude(context, id + "F5", {"entities" : qUnion([Q0]), "operationType" : NewBodyOperationType.REMOVE, "oppositeDirection" : true, "depth" : 25 * mm});
        }
        {
            var Q0;
            Q0=makeQuery(id+"F5.boolean.opBoolean","COPY",EDGE,{"derivedFrom":makeQuery(id+"F5.opExtrude","SWEPT_EDGE",EDGE,{"disambiguationData":[OSD([sQuery(id+"F0.wireOp",EDGE,"E0"),sQuery(id+"F4.wireOp",EDGE,"E95"),sQuery(id+"F4.wireOp",EDGE,"E96")])]})});
            var Q1;
            Q1=makeQuery(id+"F5.boolean.opBoolean","COPY",EDGE,{"derivedFrom":makeQuery(id+"F5.opExtrude","SWEPT_EDGE",EDGE,{"disambiguationData":[OSD([sQuery(id+"F0.wireOp",EDGE,"E0"),sQuery(id+"F4.wireOp",EDGE,"E94"),sQuery(id+"F4.wireOp",EDGE,"E96")])]})});
            var Q2;
            Q2=makeQuery(id+"F5.boolean.opBoolean","COPY",EDGE,{"derivedFrom":makeQuery(id+"F5.opExtrude","SWEPT_EDGE",EDGE,{"disambiguationData":[OSD([sQuery(id+"F0.wireOp",EDGE,"E0"),sQuery(id+"F4.wireOp",EDGE,"E99"),sQuery(id+"F4.wireOp",EDGE,"E100")])]})});
            var Q3;
            Q3=makeQuery(id+"F5.boolean.opBoolean","COPY",EDGE,{"derivedFrom":makeQuery(id+"F5.opExtrude","SWEPT_EDGE",EDGE,{"disambiguationData":[OSD([sQuery(id+"F0.wireOp",EDGE,"E0"),sQuery(id+"F4.wireOp",EDGE,"E99"),sQuery(id+"F4.wireOp",EDGE,"E101")])]})});
            var Q4;
            Q4=makeQuery(id+"F5.boolean.opBoolean","COPY",EDGE,{"derivedFrom":makeQuery(id+"F5.opExtrude","SWEPT_EDGE",EDGE,{"disambiguationData":[OSD([sQuery(id+"F0.wireOp",EDGE,"E0"),sQuery(id+"F4.wireOp",EDGE,"E105"),sQuery(id+"F4.wireOp",EDGE,"E107")])]})});
            var Q5;
            Q5=makeQuery(id+"F5.boolean.opBoolean","COPY",EDGE,{"derivedFrom":makeQuery(id+"F5.opExtrude","SWEPT_EDGE",EDGE,{"disambiguationData":[OSD([sQuery(id+"F0.wireOp",EDGE,"E0"),sQuery(id+"F4.wireOp",EDGE,"E104"),sQuery(id+"F4.wireOp",EDGE,"E107")])]})});
            var Q6;
            Q6=makeQuery(id+"F5.boolean.opBoolean","COPY",EDGE,{"derivedFrom":makeQuery(id+"F5.opExtrude","SWEPT_EDGE",EDGE,{"disambiguationData":[OSD([sQuery(id+"F0.wireOp",EDGE,"E0"),sQuery(id+"F4.wireOp",EDGE,"E103"),sQuery(id+"F4.wireOp",EDGE,"E109")])]})});
            var Q7;
            Q7=makeQuery(id+"F5.boolean.opBoolean","COPY",EDGE,{"derivedFrom":makeQuery(id+"F5.opExtrude","SWEPT_EDGE",EDGE,{"disambiguationData":[OSD([sQuery(id+"F0.wireOp",EDGE,"E0"),sQuery(id+"F4.wireOp",EDGE,"E102"),sQuery(id+"F4.wireOp",EDGE,"E109")])]})});
            var Q8;
            Q8=makeQuery(id+"F5.boolean.opBoolean","COPY",EDGE,{"derivedFrom":makeQuery(id+"F5.opExtrude","SWEPT_EDGE",EDGE,{"disambiguationData":[OSD([sQuery(id+"F4.wireOp",EDGE,"E110.1.0.13"),sQuery(id+"F4.wireOp",EDGE,"E110.1.0.15")])]})});
            var Q9;
            Q9=makeQuery(id+"F5.boolean.opBoolean","COPY",EDGE,{"derivedFrom":makeQuery(id+"F5.opExtrude","SWEPT_EDGE",EDGE,{"disambiguationData":[OSD([sQuery(id+"F4.wireOp",EDGE,"E110.1.0.14"),sQuery(id+"F4.wireOp",EDGE,"E110.1.0.15")])]})});
            var Q10;
            Q10=makeQuery(id+"F5.boolean.opBoolean","COPY",EDGE,{"derivedFrom":makeQuery(id+"F5.opExtrude","SWEPT_EDGE",EDGE,{"disambiguationData":[OSD([sQuery(id+"F4.wireOp",EDGE,"E110.1.0.10"),sQuery(id+"F4.wireOp",EDGE,"E110.1.0.11")])]})});
            var Q11;
            Q11=makeQuery(id+"F5.boolean.opBoolean","COPY",EDGE,{"derivedFrom":makeQuery(id+"F5.opExtrude","SWEPT_EDGE",EDGE,{"disambiguationData":[OSD([sQuery(id+"F4.wireOp",EDGE,"E110.1.0.8"),sQuery(id+"F4.wireOp",EDGE,"E110.1.0.11")])]})});
            var Q12;
            Q12=makeQuery(id+"F5.boolean.opBoolean","COPY",EDGE,{"derivedFrom":makeQuery(id+"F5.opExtrude","SWEPT_EDGE",EDGE,{"disambiguationData":[OSD([sQuery(id+"F4.wireOp",EDGE,"E110.1.0.6"),sQuery(id+"F4.wireOp",EDGE,"E110.1.0.7")])]})});
            var Q13;
            Q13=makeQuery(id+"F5.boolean.opBoolean","COPY",EDGE,{"derivedFrom":makeQuery(id+"F5.opExtrude","SWEPT_EDGE",EDGE,{"disambiguationData":[OSD([sQuery(id+"F4.wireOp",EDGE,"E110.1.0.5"),sQuery(id+"F4.wireOp",EDGE,"E110.1.0.7")])]})});
            var Q14;
            Q14=makeQuery(id+"F5.boolean.opBoolean","COPY",EDGE,{"derivedFrom":makeQuery(id+"F5.opExtrude","SWEPT_EDGE",EDGE,{"disambiguationData":[OSD([sQuery(id+"F4.wireOp",EDGE,"E110.1.0.0"),sQuery(id+"F4.wireOp",EDGE,"E110.1.0.1")])]})});
            var Q15;
            Q15=makeQuery(id+"F5.boolean.opBoolean","COPY",EDGE,{"derivedFrom":makeQuery(id+"F5.opExtrude","SWEPT_EDGE",EDGE,{"disambiguationData":[OSD([sQuery(id+"F4.wireOp",EDGE,"E110.1.0.1"),sQuery(id+"F4.wireOp",EDGE,"E110.1.0.2")])]})});
            var Q16;
            Q16=makeQuery(id+"F5.boolean.opBoolean","COPY",EDGE,{"derivedFrom":makeQuery(id+"F5.opExtrude","SWEPT_EDGE",EDGE,{"disambiguationData":[OSD([sQuery(id+"F4.wireOp",EDGE,"E111.1.0.2"),sQuery(id+"F4.wireOp",EDGE,"E111.1.0.3")])]})});
            var Q17;
            Q17=makeQuery(id+"F5.boolean.opBoolean","COPY",EDGE,{"derivedFrom":makeQuery(id+"F5.opExtrude","SWEPT_EDGE",EDGE,{"disambiguationData":[OSD([sQuery(id+"F4.wireOp",EDGE,"E111.1.0.1"),sQuery(id+"F4.wireOp",EDGE,"E111.1.0.2")])]})});
            var Q18;
            Q18=makeQuery(id+"F5.boolean.opBoolean","COPY",EDGE,{"derivedFrom":makeQuery(id+"F5.opExtrude","SWEPT_EDGE",EDGE,{"disambiguationData":[OSD([sQuery(id+"F4.wireOp",EDGE,"E111.1.0.5"),sQuery(id+"F4.wireOp",EDGE,"E111.1.0.6")])]})});
            var Q19;
            Q19=makeQuery(id+"F5.boolean.opBoolean","COPY",EDGE,{"derivedFrom":makeQuery(id+"F5.opExtrude","SWEPT_EDGE",EDGE,{"disambiguationData":[OSD([sQuery(id+"F4.wireOp",EDGE,"E111.1.0.6"),sQuery(id+"F4.wireOp",EDGE,"E111.1.0.7")])]})});
            var Q20;
            Q20=makeQuery(id+"F5.boolean.opBoolean","COPY",EDGE,{"derivedFrom":makeQuery(id+"F5.opExtrude","SWEPT_EDGE",EDGE,{"disambiguationData":[OSD([sQuery(id+"F4.wireOp",EDGE,"E111.1.0.8"),sQuery(id+"F4.wireOp",EDGE,"E111.1.0.11")])]})});
            var Q21;
            Q21=makeQuery(id+"F5.boolean.opBoolean","COPY",EDGE,{"derivedFrom":makeQuery(id+"F5.opExtrude","SWEPT_EDGE",EDGE,{"disambiguationData":[OSD([sQuery(id+"F4.wireOp",EDGE,"E111.1.0.10"),sQuery(id+"F4.wireOp",EDGE,"E111.1.0.11")])]})});
            var Q22;
            Q22=makeQuery(id+"F5.boolean.opBoolean","COPY",EDGE,{"derivedFrom":makeQuery(id+"F5.opExtrude","SWEPT_EDGE",EDGE,{"disambiguationData":[OSD([sQuery(id+"F4.wireOp",EDGE,"E111.1.0.14"),sQuery(id+"F4.wireOp",EDGE,"E111.1.0.15")])]})});
            var Q23;
            Q23=makeQuery(id+"F5.boolean.opBoolean","COPY",EDGE,{"derivedFrom":makeQuery(id+"F5.opExtrude","SWEPT_EDGE",EDGE,{"disambiguationData":[OSD([sQuery(id+"F4.wireOp",EDGE,"E111.1.0.13"),sQuery(id+"F4.wireOp",EDGE,"E111.1.0.14")])]})});
            var Q24;
            Q24=makeQuery(id+"F5.boolean.opBoolean","COPY",EDGE,{"derivedFrom":makeQuery(id+"F5.opExtrude","SWEPT_EDGE",EDGE,{"disambiguationData":[OSD([sQuery(id+"F4.wireOp",EDGE,"E225.MirrorCS"),sQuery(id+"F4.wireOp",EDGE,"E226.MirrorCS")])]})});
            var Q25;
            Q25=makeQuery(id+"F5.boolean.opBoolean","COPY",EDGE,{"derivedFrom":makeQuery(id+"F5.opExtrude","SWEPT_EDGE",EDGE,{"disambiguationData":[OSD([sQuery(id+"F4.wireOp",EDGE,"E221.MirrorCS"),sQuery(id+"F4.wireOp",EDGE,"E222.MirrorCS")])]})});
            var Q26;
            Q26=makeQuery(id+"F5.boolean.opBoolean","COPY",EDGE,{"derivedFrom":makeQuery(id+"F5.opExtrude","SWEPT_EDGE",EDGE,{"disambiguationData":[OSD([sQuery(id+"F4.wireOp",EDGE,"E224.MirrorCS"),sQuery(id+"F4.wireOp",EDGE,"E225.MirrorCS")])]})});
            var Q27;
            Q27=makeQuery(id+"F5.boolean.opBoolean","COPY",EDGE,{"derivedFrom":makeQuery(id+"F5.opExtrude","SWEPT_EDGE",EDGE,{"disambiguationData":[OSD([sQuery(id+"F4.wireOp",EDGE,"E211.MirrorCS"),sQuery(id+"F4.wireOp",EDGE,"E214.MirrorCS")])]})});
            var Q28;
            Q28=makeQuery(id+"F5.boolean.opBoolean","COPY",EDGE,{"derivedFrom":makeQuery(id+"F5.opExtrude","SWEPT_EDGE",EDGE,{"disambiguationData":[OSD([sQuery(id+"F4.wireOp",EDGE,"E211.MirrorCS"),sQuery(id+"F4.wireOp",EDGE,"E212.MirrorCS")])]})});
            var Q29;
            Q29=makeQuery(id+"F5.boolean.opBoolean","COPY",EDGE,{"derivedFrom":makeQuery(id+"F5.opExtrude","SWEPT_EDGE",EDGE,{"disambiguationData":[OSD([sQuery(id+"F4.wireOp",EDGE,"E216.MirrorCS"),sQuery(id+"F4.wireOp",EDGE,"E215.MirrorCS")])]})});
            var Q30;
            Q30=makeQuery(id+"F5.boolean.opBoolean","COPY",EDGE,{"derivedFrom":makeQuery(id+"F5.opExtrude","SWEPT_EDGE",EDGE,{"disambiguationData":[OSD([sQuery(id+"F4.wireOp",EDGE,"E216.MirrorCS"),sQuery(id+"F4.wireOp",EDGE,"E217.MirrorCS")])]})});
            var Q31;
            Q31=makeQuery(id+"F5.boolean.opBoolean","COPY",EDGE,{"derivedFrom":makeQuery(id+"F5.opExtrude","SWEPT_EDGE",EDGE,{"disambiguationData":[OSD([sQuery(id+"F4.wireOp",EDGE,"E219.MirrorCS"),sQuery(id+"F4.wireOp",EDGE,"E222.MirrorCS")])]})});
            var Q32;
            Q32=makeQuery(id+"F5.boolean.opBoolean","COPY",EDGE,{"derivedFrom":makeQuery(id+"F5.opExtrude","SWEPT_EDGE",EDGE,{"disambiguationData":[OSD([sQuery(id+"F4.wireOp",EDGE,"E199.MirrorCS"),sQuery(id+"F4.wireOp",EDGE,"E202.MirrorCS")])]})});
            var Q33;
            Q33=makeQuery(id+"F5.boolean.opBoolean","COPY",EDGE,{"derivedFrom":makeQuery(id+"F5.opExtrude","SWEPT_EDGE",EDGE,{"disambiguationData":[OSD([sQuery(id+"F4.wireOp",EDGE,"E196.MirrorCS"),sQuery(id+"F4.wireOp",EDGE,"E197.MirrorCS")])]})});
            var Q34;
            Q34=makeQuery(id+"F5.boolean.opBoolean","COPY",EDGE,{"derivedFrom":makeQuery(id+"F5.opExtrude","SWEPT_EDGE",EDGE,{"disambiguationData":[OSD([sQuery(id+"F4.wireOp",EDGE,"E201.MirrorCS"),sQuery(id+"F4.wireOp",EDGE,"E202.MirrorCS")])]})});
            var Q35;
            Q35=makeQuery(id+"F5.boolean.opBoolean","COPY",EDGE,{"derivedFrom":makeQuery(id+"F5.opExtrude","SWEPT_EDGE",EDGE,{"disambiguationData":[OSD([sQuery(id+"F4.wireOp",EDGE,"E203.MirrorCS"),sQuery(id+"F4.wireOp",EDGE,"E206.MirrorCS")])]})});
            var Q36;
            Q36=makeQuery(id+"F5.boolean.opBoolean","COPY",EDGE,{"derivedFrom":makeQuery(id+"F5.opExtrude","SWEPT_EDGE",EDGE,{"disambiguationData":[OSD([sQuery(id+"F4.wireOp",EDGE,"E205.MirrorCS"),sQuery(id+"F4.wireOp",EDGE,"E206.MirrorCS")])]})});
            var Q37;
            Q37=makeQuery(id+"F5.boolean.opBoolean","COPY",EDGE,{"derivedFrom":makeQuery(id+"F5.opExtrude","SWEPT_EDGE",EDGE,{"disambiguationData":[OSD([sQuery(id+"F4.wireOp",EDGE,"E209.MirrorCS"),sQuery(id+"F4.wireOp",EDGE,"E210.MirrorCS")])]})});
            var Q38;
            Q38=makeQuery(id+"F5.boolean.opBoolean","COPY",EDGE,{"derivedFrom":makeQuery(id+"F5.opExtrude","SWEPT_EDGE",EDGE,{"disambiguationData":[OSD([sQuery(id+"F4.wireOp",EDGE,"E208.MirrorCS"),sQuery(id+"F4.wireOp",EDGE,"E210.MirrorCS")])]})});
            var Q39;
            Q39=makeQuery(id+"F5.boolean.opBoolean","COPY",EDGE,{"derivedFrom":makeQuery(id+"F5.opExtrude","SWEPT_EDGE",EDGE,{"disambiguationData":[OSD([sQuery(id+"F4.wireOp",EDGE,"E196.MirrorCS"),sQuery(id+"F4.wireOp",EDGE,"E227")])]})});
            var Q40;
            Q40=makeQuery(id+"F5.boolean.opBoolean","COPY",EDGE,{"derivedFrom":makeQuery(id+"F5.opExtrude","SWEPT_EDGE",EDGE,{"disambiguationData":[OSD([sQuery(id+"F4.wireOp",EDGE,"E189.MirrorCS"),sQuery(id+"F4.wireOp",EDGE,"E190.MirrorCS")])]})});
            var Q41;
            Q41=makeQuery(id+"F5.boolean.opBoolean","COPY",EDGE,{"derivedFrom":makeQuery(id+"F5.opExtrude","SWEPT_EDGE",EDGE,{"disambiguationData":[OSD([sQuery(id+"F4.wireOp",EDGE,"E185.MirrorCS"),sQuery(id+"F4.wireOp",EDGE,"E186.MirrorCS")])]})});
            var Q42;
            Q42=makeQuery(id+"F5.boolean.opBoolean","COPY",EDGE,{"derivedFrom":makeQuery(id+"F5.opExtrude","SWEPT_EDGE",EDGE,{"disambiguationData":[OSD([sQuery(id+"F4.wireOp",EDGE,"E194.MirrorCS"),sQuery(id+"F4.wireOp",EDGE,"E195.MirrorCS")])]})});
            var Q43;
            Q43=makeQuery(id+"F5.boolean.opBoolean","COPY",EDGE,{"derivedFrom":makeQuery(id+"F5.opExtrude","SWEPT_EDGE",EDGE,{"disambiguationData":[OSD([sQuery(id+"F4.wireOp",EDGE,"E190.MirrorCS"),sQuery(id+"F4.wireOp",EDGE,"E191.MirrorCS")])]})});
            var Q44;
            Q44=makeQuery(id+"F5.boolean.opBoolean","COPY",EDGE,{"derivedFrom":makeQuery(id+"F5.opExtrude","SWEPT_EDGE",EDGE,{"disambiguationData":[OSD([sQuery(id+"F4.wireOp",EDGE,"E180.MirrorCS"),sQuery(id+"F4.wireOp",EDGE,"E183.MirrorCS")])]})});
            var Q45;
            Q45=makeQuery(id+"F5.boolean.opBoolean","COPY",EDGE,{"derivedFrom":makeQuery(id+"F5.opExtrude","SWEPT_EDGE",EDGE,{"disambiguationData":[OSD([sQuery(id+"F4.wireOp",EDGE,"E193.MirrorCS"),sQuery(id+"F4.wireOp",EDGE,"E194.MirrorCS")])]})});
            var Q46;
            Q46=makeQuery(id+"F5.boolean.opBoolean","COPY",EDGE,{"derivedFrom":makeQuery(id+"F5.opExtrude","SWEPT_EDGE",EDGE,{"disambiguationData":[OSD([sQuery(id+"F4.wireOp",EDGE,"E180.MirrorCS"),sQuery(id+"F4.wireOp",EDGE,"E181.MirrorCS")])]})});
            var Q47;
            Q47=makeQuery(id+"F5.boolean.opBoolean","COPY",EDGE,{"derivedFrom":makeQuery(id+"F5.opExtrude","SWEPT_EDGE",EDGE,{"disambiguationData":[OSD([sQuery(id+"F4.wireOp",EDGE,"E184.MirrorCS"),sQuery(id+"F4.wireOp",EDGE,"E185.MirrorCS")])]})});
            var Q48;
            Q48=makeQuery(id+"F5.boolean.opBoolean","COPY",EDGE,{"derivedFrom":makeQuery(id+"F5.opExtrude","SWEPT_EDGE",EDGE,{"disambiguationData":[OSD([sQuery(id+"F4.wireOp",EDGE,"E174.MirrorCS"),sQuery(id+"F4.wireOp",EDGE,"E175.MirrorCS")])]})});
            var Q49;
            Q49=makeQuery(id+"F5.boolean.opBoolean","COPY",EDGE,{"derivedFrom":makeQuery(id+"F5.opExtrude","SWEPT_EDGE",EDGE,{"disambiguationData":[OSD([sQuery(id+"F4.wireOp",EDGE,"E178.MirrorCS"),sQuery(id+"F4.wireOp",EDGE,"E179.MirrorCS")])]})});
            var Q50;
            Q50=makeQuery(id+"F5.boolean.opBoolean","COPY",EDGE,{"derivedFrom":makeQuery(id+"F5.opExtrude","SWEPT_EDGE",EDGE,{"disambiguationData":[OSD([sQuery(id+"F4.wireOp",EDGE,"E158.MirrorCS"),sQuery(id+"F4.wireOp",EDGE,"E159.MirrorCS")])]})});
            var Q51;
            Q51=makeQuery(id+"F5.boolean.opBoolean","COPY",EDGE,{"derivedFrom":makeQuery(id+"F5.opExtrude","SWEPT_EDGE",EDGE,{"disambiguationData":[OSD([sQuery(id+"F4.wireOp",EDGE,"E162.MirrorCS"),sQuery(id+"F4.wireOp",EDGE,"E163.MirrorCS")])]})});
            var Q52;
            Q52=makeQuery(id+"F5.boolean.opBoolean","COPY",EDGE,{"derivedFrom":makeQuery(id+"F5.opExtrude","SWEPT_EDGE",EDGE,{"disambiguationData":[OSD([sQuery(id+"F4.wireOp",EDGE,"E132.MirrorCS"),sQuery(id+"F4.wireOp",EDGE,"E133.MirrorCS")])]})});
            var Q53;
            Q53=makeQuery(id+"F5.boolean.opBoolean","COPY",EDGE,{"derivedFrom":makeQuery(id+"F5.opExtrude","SWEPT_EDGE",EDGE,{"disambiguationData":[OSD([sQuery(id+"F4.wireOp",EDGE,"E140.MirrorCS"),sQuery(id+"F4.wireOp",EDGE,"E141.MirrorCS")])]})});
            var Q54;
            Q54=makeQuery(id+"F5.boolean.opBoolean","COPY",EDGE,{"derivedFrom":makeQuery(id+"F5.opExtrude","SWEPT_EDGE",EDGE,{"disambiguationData":[OSD([sQuery(id+"F4.wireOp",EDGE,"E172.MirrorCS"),sQuery(id+"F4.wireOp",EDGE,"E175.MirrorCS")])]})});
            var Q55;
            Q55=makeQuery(id+"F5.boolean.opBoolean","COPY",EDGE,{"derivedFrom":makeQuery(id+"F5.opExtrude","SWEPT_EDGE",EDGE,{"disambiguationData":[OSD([sQuery(id+"F4.wireOp",EDGE,"E170.MirrorCS"),sQuery(id+"F4.wireOp",EDGE,"E171.MirrorCS")])]})});
            var Q56;
            Q56=makeQuery(id+"F5.boolean.opBoolean","COPY",EDGE,{"derivedFrom":makeQuery(id+"F5.opExtrude","SWEPT_EDGE",EDGE,{"disambiguationData":[OSD([sQuery(id+"F4.wireOp",EDGE,"E160.MirrorCS"),sQuery(id+"F4.wireOp",EDGE,"E163.MirrorCS")])]})});
            var Q57;
            Q57=makeQuery(id+"F5.boolean.opBoolean","COPY",EDGE,{"derivedFrom":makeQuery(id+"F5.opExtrude","SWEPT_EDGE",EDGE,{"disambiguationData":[OSD([sQuery(id+"F4.wireOp",EDGE,"E153.MirrorCS"),sQuery(id+"F4.wireOp",EDGE,"E154.MirrorCS")])]})});
            var Q58;
            Q58=makeQuery(id+"F5.boolean.opBoolean","COPY",EDGE,{"derivedFrom":makeQuery(id+"F5.opExtrude","SWEPT_EDGE",EDGE,{"disambiguationData":[OSD([sQuery(id+"F4.wireOp",EDGE,"E132.MirrorCS"),sQuery(id+"F4.wireOp",EDGE,"E135.MirrorCS")])]})});
            var Q59;
            Q59=makeQuery(id+"F5.boolean.opBoolean","COPY",EDGE,{"derivedFrom":makeQuery(id+"F5.opExtrude","SWEPT_EDGE",EDGE,{"disambiguationData":[OSD([sQuery(id+"F4.wireOp",EDGE,"E137.MirrorCS"),sQuery(id+"F4.wireOp",EDGE,"E139.MirrorCS")])]})});
            var Q60;
            Q60=makeQuery(id+"F5.boolean.opBoolean","COPY",EDGE,{"derivedFrom":makeQuery(id+"F5.opExtrude","SWEPT_EDGE",EDGE,{"disambiguationData":[OSD([sQuery(id+"F4.wireOp",EDGE,"E169.MirrorCS"),sQuery(id+"F4.wireOp",EDGE,"E170.MirrorCS")])]})});
            var Q61;
            Q61=makeQuery(id+"F5.boolean.opBoolean","COPY",EDGE,{"derivedFrom":makeQuery(id+"F5.opExtrude","SWEPT_EDGE",EDGE,{"disambiguationData":[OSD([sQuery(id+"F4.wireOp",EDGE,"E164.MirrorCS"),sQuery(id+"F4.wireOp",EDGE,"E165.MirrorCS")])]})});
            var Q62;
            Q62=makeQuery(id+"F5.boolean.opBoolean","COPY",EDGE,{"derivedFrom":makeQuery(id+"F5.opExtrude","SWEPT_EDGE",EDGE,{"disambiguationData":[OSD([sQuery(id+"F4.wireOp",EDGE,"E152.MirrorCS"),sQuery(id+"F4.wireOp",EDGE,"E153.MirrorCS")])]})});
            var Q63;
            Q63=makeQuery(id+"F5.boolean.opBoolean","COPY",EDGE,{"derivedFrom":makeQuery(id+"F5.opExtrude","SWEPT_EDGE",EDGE,{"disambiguationData":[OSD([sQuery(id+"F4.wireOp",EDGE,"E148.MirrorCS"),sQuery(id+"F4.wireOp",EDGE,"E150.MirrorCS")])]})});
            var Q64;
            Q64=makeQuery(id+"F5.boolean.opBoolean","COPY",EDGE,{"derivedFrom":makeQuery(id+"F5.opExtrude","SWEPT_EDGE",EDGE,{"disambiguationData":[OSD([sQuery(id+"F4.wireOp",EDGE,"E137.MirrorCS"),sQuery(id+"F4.wireOp",EDGE,"E138.MirrorCS")])]})});
            var Q65;
            Q65=makeQuery(id+"F5.boolean.opBoolean","COPY",EDGE,{"derivedFrom":makeQuery(id+"F5.opExtrude","SWEPT_EDGE",EDGE,{"disambiguationData":[OSD([sQuery(id+"F4.wireOp",EDGE,"E146.MirrorCS"),sQuery(id+"F4.wireOp",EDGE,"E147.MirrorCS")])]})});
            var Q66;
            Q66=makeQuery(id+"F5.boolean.opBoolean","COPY",EDGE,{"derivedFrom":makeQuery(id+"F5.opExtrude","SWEPT_EDGE",EDGE,{"disambiguationData":[OSD([sQuery(id+"F4.wireOp",EDGE,"E176.MirrorCS"),sQuery(id+"F4.wireOp",EDGE,"E179.MirrorCS")])]})});
            var Q67;
            Q67=makeQuery(id+"F5.boolean.opBoolean","COPY",EDGE,{"derivedFrom":makeQuery(id+"F5.opExtrude","SWEPT_EDGE",EDGE,{"disambiguationData":[OSD([sQuery(id+"F4.wireOp",EDGE,"E165.MirrorCS"),sQuery(id+"F4.wireOp",EDGE,"E166.MirrorCS")])]})});
            var Q68;
            Q68=makeQuery(id+"F5.boolean.opBoolean","COPY",EDGE,{"derivedFrom":makeQuery(id+"F5.opExtrude","SWEPT_EDGE",EDGE,{"disambiguationData":[OSD([sQuery(id+"F4.wireOp",EDGE,"E157.MirrorCS"),sQuery(id+"F4.wireOp",EDGE,"E159.MirrorCS")])]})});
            var Q69;
            Q69=makeQuery(id+"F5.boolean.opBoolean","COPY",EDGE,{"derivedFrom":makeQuery(id+"F5.opExtrude","SWEPT_EDGE",EDGE,{"disambiguationData":[OSD([sQuery(id+"F4.wireOp",EDGE,"E150.MirrorCS"),sQuery(id+"F4.wireOp",EDGE,"E151.MirrorCS")])]})});
            var Q70;
            Q70=makeQuery(id+"F5.boolean.opBoolean","COPY",EDGE,{"derivedFrom":makeQuery(id+"F5.opExtrude","SWEPT_EDGE",EDGE,{"disambiguationData":[OSD([sQuery(id+"F4.wireOp",EDGE,"E141.MirrorCS"),sQuery(id+"F4.wireOp",EDGE,"E142.MirrorCS")])]})});
            var Q71;
            Q71=makeQuery(id+"F5.boolean.opBoolean","COPY",EDGE,{"derivedFrom":makeQuery(id+"F5.opExtrude","SWEPT_EDGE",EDGE,{"disambiguationData":[OSD([sQuery(id+"F4.wireOp",EDGE,"E145.MirrorCS"),sQuery(id+"F4.wireOp",EDGE,"E147.MirrorCS")])]})});
            fillet(context, id + "F6", {"entities" : qUnion([Q0, Q1, Q2, Q3, Q4, Q5, Q6, Q7, Q8, Q9, Q10, Q11, Q12, Q13, Q14, Q15, Q16, Q17, Q18, Q19, Q20, Q21, Q22, Q23, Q24, Q25, Q26, Q27, Q28, Q29, Q30, Q31, Q32, Q33, Q34, Q35, Q36, Q37, Q38, Q39, Q40, Q41, Q42, Q43, Q44, Q45, Q46, Q47, Q48, Q49, Q50, Q51, Q52, Q53, Q54, Q55, Q56, Q57, Q58, Q59, Q60, Q61, Q62, Q63, Q64, Q65, Q66, Q67, Q68, Q69, Q70, Q71]), "radius" : 1 * mm, "tangentPropagation" : true, "allowEdgeOverflow" : false});
        }
        {
            var Q0;
            Q0=makeQuery(id+"F1.opExtrude","CAP_FACE",FACE,{"disambiguationData":[OSD([sQuery(id+"F0.wireOp",EDGE,"E31.0"),sQuery(id+"F0.wireOp",EDGE,"E31.1"),sQuery(id+"F0.wireOp",EDGE,"E31.2"),sQuery(id+"F0.wireOp",EDGE,"E31.3"),sQuery(id+"F0.wireOp",EDGE,"E32.filletArc"),sQuery(id+"F0.wireOp",EDGE,"E33.filletArc"),sQuery(id+"F0.wireOp",EDGE,"E34.filletArc"),sQuery(id+"F0.wireOp",EDGE,"E35.filletArc"),sQuery(id+"F0.wireOp",EDGE,"E49"),sQuery(id+"F0.wireOp",EDGE,"E50"),sQuery(id+"F0.wireOp",EDGE,"E51"),sQuery(id+"F0.wireOp",EDGE,"E52"),sQuery(id+"F0.wireOp",EDGE,"E53"),sQuery(id+"F0.wireOp",EDGE,"E54"),sQuery(id+"F0.wireOp",EDGE,"E55"),sQuery(id+"F0.wireOp",EDGE,"E56"),sQuery(id+"F0.wireOp",EDGE,"E57"),sQuery(id+"F0.wireOp",EDGE,"E58"),sQuery(id+"F0.wireOp",EDGE,"E59"),sQuery(id+"F0.wireOp",EDGE,"E60")])],"isStart":true});
            var sketch = newSketch(context, id + "F7", { "sketchPlane" : qUnion([Q0])});
            skLineSegment(sketch, "E228.0", {"start": v(-15, 24) * mm, "end": v(15, 24) * mm, "construction": true});
            skLineSegment(sketch, "E229.0", {"start": v(-15, -24) * mm, "end": v(15, -24) * mm, "construction": true});
            skLineSegment(sketch, "E230.0", {"start": v(-24, -15) * mm, "end": v(-24, 15) * mm, "construction": true});
            skLineSegment(sketch, "E231.0", {"start": v(24, 15) * mm, "end": v(24, -15) * mm, "construction": true});
            skArc(sketch, "E232.0", {"start": v(-24, 15) * mm, "mid": v(-21.36, 21.36) * mm, "end": v(-15, 24) * mm, "construction": true});
            skArc(sketch, "E233.0", {"start": v(-15, -24) * mm, "mid": v(-21.36, -21.36) * mm, "end": v(-24, -15) * mm, "construction": true});
            skArc(sketch, "E234.0", {"start": v(24, -15) * mm, "mid": v(21.36, -21.36) * mm, "end": v(15, -24) * mm, "construction": true});
            skArc(sketch, "E235.0", {"start": v(15, 24) * mm, "mid": v(21.36, 21.36) * mm, "end": v(24, 15) * mm, "construction": true});
            skLineSegment(sketch, "E236", {"start": v(0, 0) * mm, "end": v(0, -24) * mm, "construction": true});
            skLineSegment(sketch, "E237", {"start": v(0, -24) * mm, "end": v(0, -48) * mm, "construction": true});
            skLineSegment(sketch, "E238", {"start": v(0, -48) * mm, "end": v(0, -72) * mm, "construction": true});
            skLineSegment(sketch, "E239", {"start": v(-24, -15) * mm, "end": v(-24, -24) * mm, "construction": true});
            skLineSegment(sketch, "E240", {"start": v(-24, -24) * mm, "end": v(-15, -24) * mm, "construction": true});
            skLineSegment(sketch, "E241", {"start": v(24, -15) * mm, "end": v(24, -24) * mm, "construction": true});
            skLineSegment(sketch, "E242", {"start": v(24, -24) * mm, "end": v(15, -24) * mm, "construction": true});
            skLineSegment(sketch, "E243", {"start": v(24, -24) * mm, "end": v(24, -72) * mm, "construction": true});
            skLineSegment(sketch, "E244", {"start": v(24, -72) * mm, "end": v(0, -72) * mm, "construction": true});
            skLineSegment(sketch, "E245", {"start": v(0, -72) * mm, "end": v(-24, -72) * mm, "construction": true});
            skLineSegment(sketch, "E246", {"start": v(-24, -72) * mm, "end": v(-24, -24) * mm, "construction": true});
            skLineSegment(sketch, "E247", {"start": v(0, -48) * mm, "end": v(-24, -48) * mm, "construction": true});
            skLineSegment(sketch, "E248", {"start": v(0, -48) * mm, "end": v(24, -48) * mm, "construction": true});
            skCircle(sketch, "E249", {"center": v(0, -48) * mm, "radius": 17.75 * mm});
            skCircle(sketch, "E250", {"center": v(0, -48) * mm, "radius": 24 * mm, "construction": true});
            skLineSegment(sketch, "E251.bottom", {"start": v(15, -24) * mm, "end": v(-15, -24) * mm});
            skLineSegment(sketch, "E251.top", {"start": v(15, -72) * mm, "end": v(-15, -72) * mm});
            skLineSegment(sketch, "E251.left", {"start": v(24, -33) * mm, "end": v(24, -63) * mm});
            skLineSegment(sketch, "E251.right", {"start": v(-24, -33) * mm, "end": v(-24, -63) * mm});
            skPoint(sketch, "E252.visualSharp", {"position": v(-24, -72) * mm});
            skArc(sketch, "E252.filletArc", {"start": v(-24, -63) * mm, "mid": v(-21.36, -69.36) * mm, "end": v(-15, -72) * mm});
            skPoint(sketch, "E253.visualSharp", {"position": v(-24, -24) * mm});
            skArc(sketch, "E253.filletArc", {"start": v(-15, -24) * mm, "mid": v(-21.36, -26.64) * mm, "end": v(-24, -33) * mm});
            skPoint(sketch, "E254.visualSharp", {"position": v(24, -72) * mm});
            skArc(sketch, "E254.filletArc", {"start": v(15, -72) * mm, "mid": v(21.36, -69.36) * mm, "end": v(24, -63) * mm});
            skPoint(sketch, "E255.visualSharp", {"position": v(24, -24) * mm});
            skArc(sketch, "E255.filletArc", {"start": v(24, -33) * mm, "mid": v(21.36, -26.64) * mm, "end": v(15, -24) * mm});
            skSolve(sketch);
        }
        {
            var Q0;
            Q0=makeQuery(id+"F7.imprint","IMPRINT",FACE,{"disambiguationData":[TD([[makeQuery(id+"F7.imprint","IMPRINT",EDGE,{"derivedFrom":sQuery(id+"F7.wireOp",EDGE,"E249")}),-1.0]])]});
            var Q1;
            Q1=makeQuery(id+"F1.opExtrude","CAP_FACE",FACE,{"disambiguationData":[OSD([sQuery(id+"F0.wireOp",EDGE,"E31.0"),sQuery(id+"F0.wireOp",EDGE,"E31.1"),sQuery(id+"F0.wireOp",EDGE,"E31.2"),sQuery(id+"F0.wireOp",EDGE,"E31.3"),sQuery(id+"F0.wireOp",EDGE,"E32.filletArc"),sQuery(id+"F0.wireOp",EDGE,"E33.filletArc"),sQuery(id+"F0.wireOp",EDGE,"E34.filletArc"),sQuery(id+"F0.wireOp",EDGE,"E35.filletArc"),sQuery(id+"F0.wireOp",EDGE,"E49"),sQuery(id+"F0.wireOp",EDGE,"E50"),sQuery(id+"F0.wireOp",EDGE,"E51"),sQuery(id+"F0.wireOp",EDGE,"E52"),sQuery(id+"F0.wireOp",EDGE,"E53"),sQuery(id+"F0.wireOp",EDGE,"E54"),sQuery(id+"F0.wireOp",EDGE,"E55"),sQuery(id+"F0.wireOp",EDGE,"E56"),sQuery(id+"F0.wireOp",EDGE,"E57"),sQuery(id+"F0.wireOp",EDGE,"E58"),sQuery(id+"F0.wireOp",EDGE,"E59"),sQuery(id+"F0.wireOp",EDGE,"E60")])],"isStart":false});
            extrude(context, id + "F8", {"entities" : qUnion([Q0]), "endBound" : BoundingType.UP_TO_SURFACE, "oppositeDirection" : true, "endBoundEntityFace" : qUnion([Q1]), "depth" : 25 * mm});
        }
        {
            var Q0;
            Q0=makeQuery(id+"F8.opExtrude","CAP_EDGE",EDGE,{"disambiguationData":[OSD([sQuery(id+"F7.wireOp",EDGE,"E251.right")])],"isStart":true});
            var Q1;
            Q1=makeQuery(id+"F8.opExtrude","CAP_EDGE",EDGE,{"disambiguationData":[OSD([sQuery(id+"F7.wireOp",EDGE,"E249")])],"isStart":true});
            fillet(context, id + "F9", {"entities" : qUnion([Q0, Q1]), "radius" : 2.5 * mm, "tangentPropagation" : true, "allowEdgeOverflow" : false});
        }
        {
            var Q0;
            Q0=makeQuery(id+"F8.opExtrude","CAP_FACE",FACE,{"disambiguationData":[OSD([sQuery(id+"F7.wireOp",EDGE,"E249"),sQuery(id+"F7.wireOp",EDGE,"E251.bottom"),sQuery(id+"F7.wireOp",EDGE,"E251.top"),sQuery(id+"F7.wireOp",EDGE,"E251.left"),sQuery(id+"F7.wireOp",EDGE,"E251.right"),sQuery(id+"F7.wireOp",EDGE,"E252.filletArc"),sQuery(id+"F7.wireOp",EDGE,"E253.filletArc"),sQuery(id+"F7.wireOp",EDGE,"E254.filletArc"),sQuery(id+"F7.wireOp",EDGE,"E255.filletArc")])],"isStart":true});
            var sketch = newSketch(context, id + "F10", { "sketchPlane" : qUnion([Q0])});
            skArc(sketch, "E256.0", {"start": v(-24, -33) * mm, "mid": v(-21.36, -26.64) * mm, "end": v(-15, -24) * mm, "construction": true});
            skLineSegment(sketch, "E257.0", {"start": v(-24, -63) * mm, "end": v(-24, -33) * mm, "construction": true});
            skArc(sketch, "E258.0", {"start": v(-15, -72) * mm, "mid": v(-21.36, -69.36) * mm, "end": v(-24, -63) * mm, "construction": true});
            skLineSegment(sketch, "E259.0", {"start": v(15, -72) * mm, "end": v(-15, -72) * mm, "construction": true});
            skArc(sketch, "E260.0", {"start": v(24, -63) * mm, "mid": v(21.36, -69.36) * mm, "end": v(15, -72) * mm, "construction": true});
            skLineSegment(sketch, "E261.0", {"start": v(24, -63) * mm, "end": v(24, -33) * mm, "construction": true});
            skArc(sketch, "E262.0", {"start": v(15, -24) * mm, "mid": v(21.36, -26.64) * mm, "end": v(24, -33) * mm, "construction": true});
            skLineSegment(sketch, "E263.0", {"start": v(-15, -24) * mm, "end": v(15, -24) * mm, "construction": true});
            skCircle(sketch, "E264.0", {"center": v(0, -48) * mm, "radius": 17.75 * mm, "construction": true});
            skLineSegment(sketch, "E265", {"start": v(0, -48) * mm, "end": v(-21.36, -26.64) * mm, "construction": true});
            skLineSegment(sketch, "E266", {"start": v(0, -48) * mm, "end": v(21.36, -26.64) * mm, "construction": true});
            skLineSegment(sketch, "E267", {"start": v(0, -48) * mm, "end": v(-21.36, -69.36) * mm, "construction": true});
            skLineSegment(sketch, "E268", {"start": v(0, -48) * mm, "end": v(21.36, -69.36) * mm, "construction": true});
            skLineSegment(sketch, "E269", {"start": v(12.55, -60.55) * mm, "end": v(21.36, -69.36) * mm, "construction": true});
            skLineSegment(sketch, "E270", {"start": v(-12.55, -60.55) * mm, "end": v(-21.36, -69.36) * mm, "construction": true});
            skLineSegment(sketch, "E271", {"start": v(-21.36, -26.64) * mm, "end": v(-12.55, -35.45) * mm, "construction": true});
            skLineSegment(sketch, "E272", {"start": v(21.36, -26.64) * mm, "end": v(12.55, -35.45) * mm, "construction": true});
            skCircle(sketch, "E273", {"center": v(16.96, -31.04) * mm, "radius": 1.78 * mm});
            skCircle(sketch, "E274", {"center": v(16.96, -64.96) * mm, "radius": 1.78 * mm});
            skCircle(sketch, "E275", {"center": v(-16.96, -64.96) * mm, "radius": 1.78 * mm});
            skCircle(sketch, "E276", {"center": v(-16.96, -31.04) * mm, "radius": 1.78 * mm});
            skCircle(sketch, "E277.0", {"center": v(-7, -7) * mm, "radius": 1.78 * mm, "construction": true});
            skSolve(sketch);
        }
        {
            var Q0;
            Q0 = qSketchRegion(id + "F10", true);
            extrude(context, id + "F11", {"entities" : qUnion([Q0]), "operationType" : NewBodyOperationType.REMOVE, "oppositeDirection" : true, "depth" : 25 * mm});
        }
        {
            var Q0;
            Q0=makeQuery(id+"F8.opExtrude","CAP_FACE",FACE,{"disambiguationData":[OSD([sQuery(id+"F7.wireOp",EDGE,"E249"),sQuery(id+"F7.wireOp",EDGE,"E251.bottom"),sQuery(id+"F7.wireOp",EDGE,"E251.top"),sQuery(id+"F7.wireOp",EDGE,"E251.left"),sQuery(id+"F7.wireOp",EDGE,"E251.right"),sQuery(id+"F7.wireOp",EDGE,"E252.filletArc"),sQuery(id+"F7.wireOp",EDGE,"E253.filletArc"),sQuery(id+"F7.wireOp",EDGE,"E254.filletArc"),sQuery(id+"F7.wireOp",EDGE,"E255.filletArc")])],"isStart":false});
            var sketch = newSketch(context, id + "F12", { "sketchPlane" : qUnion([Q0])});
            skLineSegment(sketch, "E278.0", {"start": v(15, -24) * mm, "end": v(-15, -24) * mm, "construction": true});
            skArc(sketch, "E279.0", {"start": v(24, -33) * mm, "mid": v(21.36, -26.64) * mm, "end": v(15, -24) * mm, "construction": true});
            skLineSegment(sketch, "E280.0", {"start": v(24, -63) * mm, "end": v(24, -33) * mm, "construction": true});
            skArc(sketch, "E281.0", {"start": v(15, -72) * mm, "mid": v(21.36, -69.36) * mm, "end": v(24, -63) * mm, "construction": true});
            skLineSegment(sketch, "E282.0", {"start": v(15, -72) * mm, "end": v(-15, -72) * mm, "construction": true});
            skArc(sketch, "E283.0", {"start": v(-24, -63) * mm, "mid": v(-21.36, -69.36) * mm, "end": v(-15, -72) * mm, "construction": true});
            skLineSegment(sketch, "E284.0", {"start": v(-24, -33) * mm, "end": v(-24, -63) * mm, "construction": true});
            skArc(sketch, "E285.0", {"start": v(-15, -24) * mm, "mid": v(-21.36, -26.64) * mm, "end": v(-24, -33) * mm, "construction": true});
            skLineSegment(sketch, "E286", {"start": v(0, -24) * mm, "end": v(0, -72) * mm, "construction": true});
            skLineSegment(sketch, "E287", {"start": v(24, -48) * mm, "end": v(0, -48) * mm, "construction": true});
            skLineSegment(sketch, "E288", {"start": v(0, -48) * mm, "end": v(-24, -48) * mm, "construction": true});
            skPoint(sketch, "E289.rect.middle", {"position": v(0, -48) * mm});
            skLineSegment(sketch, "E290", {"start": v(-5.79, -48) * mm, "end": v(-5.79, -60.5) * mm, "construction": true});
            skLineSegment(sketch, "E291.top", {"start": v(0, -60.5) * mm, "end": v(-12, -60.5) * mm});
            skLineSegment(sketch, "E291.left", {"start": v(0, -48) * mm, "end": v(0, -60.5) * mm, "construction": true});
            skLineSegment(sketch, "E291.right", {"start": v(-12, -48) * mm, "end": v(-12, -60.5) * mm});
            skLineSegment(sketch, "E292", {"start": v(-5.79, -48) * mm, "end": v(-5.79, -35.5) * mm, "construction": true});
            skLineSegment(sketch, "E293.top", {"start": v(-12, -35.5) * mm, "end": v(0, -35.5) * mm});
            skLineSegment(sketch, "E293.left", {"start": v(-12, -48) * mm, "end": v(-12, -35.5) * mm});
            skLineSegment(sketch, "E293.right", {"start": v(0, -48) * mm, "end": v(0, -35.5) * mm, "construction": true});
            skLineSegment(sketch, "E294.bottom", {"start": v(0, -60.5) * mm, "end": v(12, -60.5) * mm});
            skLineSegment(sketch, "E294.right", {"start": v(12, -60.5) * mm, "end": v(12, -48) * mm});
            skLineSegment(sketch, "E295.bottom", {"start": v(0, -35.5) * mm, "end": v(12, -35.5) * mm});
            skLineSegment(sketch, "E295.top", {"start": v(0, -48) * mm, "end": v(12, -48) * mm, "construction": true});
            skLineSegment(sketch, "E295.right", {"start": v(12, -35.5) * mm, "end": v(12, -48) * mm});
            skPoint(sketch, "E296", {"position": v(-10, -37.5) * mm});
            skLineSegment(sketch, "E297", {"start": v(-10, -37.5) * mm, "end": v(-10, -58.5) * mm, "construction": true});
            skLineSegment(sketch, "E298", {"start": v(-10, -37.5) * mm, "end": v(-10, -35.5) * mm, "construction": true});
            skLineSegment(sketch, "E299", {"start": v(-10, -37.5) * mm, "end": v(-12, -37.5) * mm, "construction": true});
            skLineSegment(sketch, "E300", {"start": v(-10, -58.5) * mm, "end": v(-10, -60.5) * mm, "construction": true});
            skLineSegment(sketch, "E301", {"start": v(-10, -37.5) * mm, "end": v(2.5, -37.5) * mm, "construction": true});
            skLineSegment(sketch, "E302", {"start": v(2.5, -37.5) * mm, "end": v(2.5, -58.5) * mm, "construction": true});
            skLineSegment(sketch, "E303", {"start": v(-10, -58.5) * mm, "end": v(2.5, -58.5) * mm, "construction": true});
            skCircle(sketch, "E304", {"center": v(-10, -37.5) * mm, "radius": 1.06 * mm});
            skCircle(sketch, "E305", {"center": v(2.5, -37.5) * mm, "radius": 1.06 * mm});
            skCircle(sketch, "E306", {"center": v(2.5, -58.5) * mm, "radius": 1.06 * mm});
            skCircle(sketch, "E307", {"center": v(-10, -58.5) * mm, "radius": 1.06 * mm});
            skSolve(sketch);
        }
        {
            var Q0;
            Q0 = qSketchRegion(id + "F12", true);
            extrude(context, id + "F13", {"entities" : qUnion([Q0]), "depth" : 1 * mm});
        }
        {
            var Q0;
            Q0=makeQuery(id+"F13.opExtrude","CAP_FACE",FACE,{"disambiguationData":[OSD([sQuery(id+"F12.wireOp",EDGE,"E291.top"),sQuery(id+"F12.wireOp",EDGE,"E291.right"),sQuery(id+"F12.wireOp",EDGE,"E293.top"),sQuery(id+"F12.wireOp",EDGE,"E293.left"),sQuery(id+"F12.wireOp",EDGE,"E294.bottom"),sQuery(id+"F12.wireOp",EDGE,"E294.right"),sQuery(id+"F12.wireOp",EDGE,"E295.bottom"),sQuery(id+"F12.wireOp",EDGE,"E295.right"),sQuery(id+"F12.wireOp",EDGE,"E304"),sQuery(id+"F12.wireOp",EDGE,"E305"),sQuery(id+"F12.wireOp",EDGE,"E306"),sQuery(id+"F12.wireOp",EDGE,"E307")])],"isStart":false});
            var sketch = newSketch(context, id + "F14", { "sketchPlane" : qUnion([Q0])});
            skLineSegment(sketch, "E308.0.0", {"start": v(-12, -60.5) * mm, "end": v(12, -60.5) * mm, "construction": true});
            skLineSegment(sketch, "E308.0.1", {"start": v(12, -60.5) * mm, "end": v(12, -35.5) * mm, "construction": true});
            skLineSegment(sketch, "E308.0.2", {"start": v(12, -35.5) * mm, "end": v(-12, -35.5) * mm, "construction": true});
            skLineSegment(sketch, "E308.0.3", {"start": v(-12, -35.5) * mm, "end": v(-12, -60.5) * mm, "construction": true});
            skLineSegment(sketch, "E309", {"start": v(2.5, -37.5) * mm, "end": v(2.5, -58.5) * mm, "construction": true});
            skLineSegment(sketch, "E310", {"start": v(2.5, -37.5) * mm, "end": v(12, -37.5) * mm, "construction": true});
            skLineSegment(sketch, "E311", {"start": v(2.5, -58.5) * mm, "end": v(12, -58.5) * mm, "construction": true});
            skLineSegment(sketch, "E312", {"start": v(12, -48) * mm, "end": v(6, -48) * mm, "construction": true});
            skLineSegment(sketch, "E313.bottom", {"start": v(6, -37.5) * mm, "end": v(12, -37.5) * mm});
            skLineSegment(sketch, "E313.top", {"start": v(6, -58.5) * mm, "end": v(12, -58.5) * mm});
            skLineSegment(sketch, "E313.left", {"start": v(6, -37.5) * mm, "end": v(6, -58.5) * mm});
            skLineSegment(sketch, "E313.right", {"start": v(12, -37.5) * mm, "end": v(12, -58.5) * mm});
            skSolve(sketch);
        }
        {
            var Q0;
            Q0 = qSketchRegion(id + "F14", true);
            extrude(context, id + "F15", {"entities" : qUnion([Q0]), "operationType" : NewBodyOperationType.ADD, "depth" : 3.75 * mm});
        }
        {
            var Q0;
            Q0=makeQuery(id+"F13.opExtrude","CAP_FACE",FACE,{"disambiguationData":[OSD([sQuery(id+"F12.wireOp",EDGE,"E291.top"),sQuery(id+"F12.wireOp",EDGE,"E291.right"),sQuery(id+"F12.wireOp",EDGE,"E293.top"),sQuery(id+"F12.wireOp",EDGE,"E293.left"),sQuery(id+"F12.wireOp",EDGE,"E294.bottom"),sQuery(id+"F12.wireOp",EDGE,"E294.right"),sQuery(id+"F12.wireOp",EDGE,"E295.bottom"),sQuery(id+"F12.wireOp",EDGE,"E295.right"),sQuery(id+"F12.wireOp",EDGE,"E304"),sQuery(id+"F12.wireOp",EDGE,"E305"),sQuery(id+"F12.wireOp",EDGE,"E306"),sQuery(id+"F12.wireOp",EDGE,"E307")])],"isStart":true});
            var sketch = newSketch(context, id + "F16", { "sketchPlane" : qUnion([Q0])});
            skLineSegment(sketch, "E314.0.0", {"start": v(-12, -60.5) * mm, "end": v(12, -60.5) * mm, "construction": true});
            skLineSegment(sketch, "E314.0.1", {"start": v(12, -60.5) * mm, "end": v(12, -35.5) * mm, "construction": true});
            skLineSegment(sketch, "E314.0.2", {"start": v(12, -35.5) * mm, "end": v(-12, -35.5) * mm, "construction": true});
            skLineSegment(sketch, "E314.0.3", {"start": v(-12, -35.5) * mm, "end": v(-12, -60.5) * mm, "construction": true});
            skLineSegment(sketch, "E315", {"start": v(-12, -48) * mm, "end": v(-6.5, -48) * mm, "construction": true});
            skLineSegment(sketch, "E316", {"start": v(-6.5, -48) * mm, "end": v(-6.5, -52) * mm});
            skLineSegment(sketch, "E317", {"start": v(-6.5, -52) * mm, "end": v(1.5, -52) * mm});
            skLineSegment(sketch, "E318", {"start": v(1.5, -52) * mm, "end": v(1.5, -48) * mm});
            skLineSegment(sketch, "E319", {"start": v(1.5, -52) * mm, "end": v(-2.5, -52) * mm, "construction": true});
            skLineSegment(sketch, "E320", {"start": v(1.5, -52) * mm, "end": v(-2.5, -48) * mm, "construction": true});
            skLineSegment(sketch, "E321", {"start": v(-2.5, -48) * mm, "end": v(-6.5, -44) * mm, "construction": true});
            skLineSegment(sketch, "E322", {"start": v(-6.5, -48) * mm, "end": v(-6.5, -44) * mm});
            skLineSegment(sketch, "E323", {"start": v(-6.5, -44) * mm, "end": v(1.5, -44) * mm});
            skLineSegment(sketch, "E324", {"start": v(1.5, -44) * mm, "end": v(1.5, -48) * mm});
            skSolve(sketch);
        }
        {
            var Q0;
            Q0=makeQuery(id+"F16.imprint","IMPRINT",FACE,{"disambiguationData":[TD([[makeQuery(id+"F16.imprint","IMPRINT",EDGE,{"derivedFrom":sQuery(id+"F16.wireOp",EDGE,"E316")}),1.0]])]});
            extrude(context, id + "F17", {"entities" : qUnion([Q0]), "operationType" : NewBodyOperationType.ADD, "depth" : 4.5 * mm});
        }
    });
